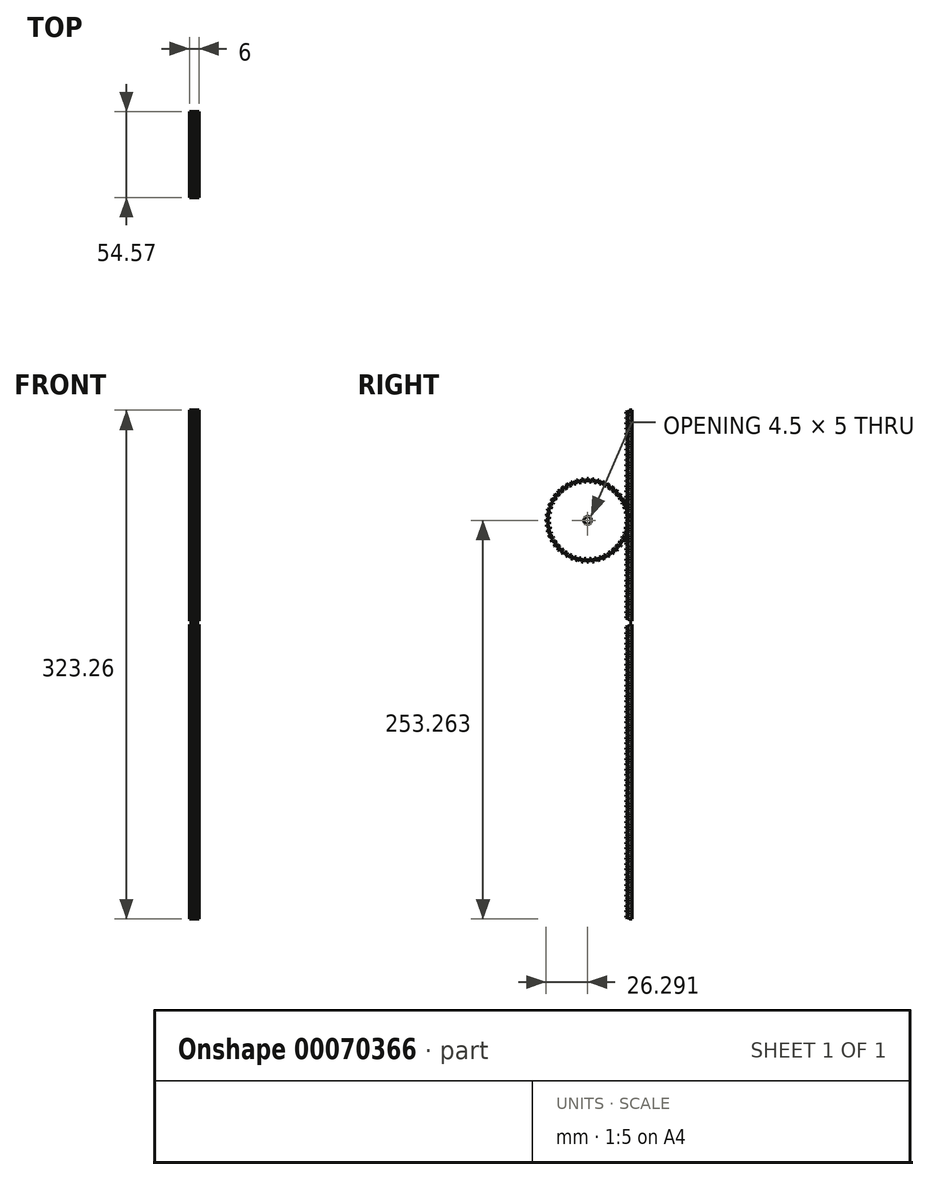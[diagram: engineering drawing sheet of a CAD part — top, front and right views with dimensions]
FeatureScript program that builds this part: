
annotation { "Feature Type Name" : "Feature", "Feature Type Description" : "" }
export const myFeature = defineFeature(function(context is Context, id is Id, definition is map)
    precondition{}
    {
        {
            var Q0;
            Q0=qCreatedBy(makeId("Right.planeOp"),FACE);
            var sketch = newSketch(context, id + "F0", { "sketchPlane" : qUnion([Q0])});
            skLineSegment(sketch, "E0", {"start": v(24.08, -5.55) * mm, "end": v(24.17, -5.13) * mm});
            skLineSegment(sketch, "E1", {"start": v(24.17, -5.13) * mm, "end": v(24.2, -4.7) * mm});
            skLineSegment(sketch, "E2", {"start": v(24.2, -4.7) * mm, "end": v(23.83, -4.49) * mm});
            skLineSegment(sketch, "E3", {"start": v(23.83, -4.49) * mm, "end": v(23.46, -4.3) * mm});
            skLineSegment(sketch, "E4", {"start": v(23.46, -4.3) * mm, "end": v(23.13, -4.14) * mm});
            skLineSegment(sketch, "E5", {"start": v(23.13, -4.14) * mm, "end": v(22.83, -4.01) * mm});
            skLineSegment(sketch, "E6", {"start": v(22.83, -4.01) * mm, "end": v(22.57, -3.91) * mm});
            skLineSegment(sketch, "E7", {"start": v(22.57, -3.91) * mm, "end": v(22.3, -3.83) * mm});
            skLineSegment(sketch, "E8", {"start": v(22.3, -3.83) * mm, "end": v(22.21, -3.78) * mm});
            skLineSegment(sketch, "E9", {"start": v(22.21, -3.78) * mm, "end": v(22.17, -3.73) * mm});
            skLineSegment(sketch, "E10", {"start": v(22.17, -3.73) * mm, "end": v(22.23, -2.79) * mm});
            skLineSegment(sketch, "E11", {"start": v(22.23, -2.79) * mm, "end": v(22.28, -2.75) * mm});
            skLineSegment(sketch, "E12", {"start": v(22.28, -2.75) * mm, "end": v(22.38, -2.71) * mm});
            skLineSegment(sketch, "E13", {"start": v(22.38, -2.71) * mm, "end": v(22.65, -2.66) * mm});
            skLineSegment(sketch, "E14", {"start": v(22.65, -2.66) * mm, "end": v(22.92, -2.6) * mm});
            skLineSegment(sketch, "E15", {"start": v(22.92, -2.6) * mm, "end": v(23.23, -2.52) * mm});
            skLineSegment(sketch, "E16", {"start": v(23.23, -2.52) * mm, "end": v(23.59, -2.4) * mm});
            skLineSegment(sketch, "E17", {"start": v(23.59, -2.4) * mm, "end": v(23.98, -2.26) * mm});
            skLineSegment(sketch, "E18", {"start": v(23.98, -2.26) * mm, "end": v(24.36, -2.1) * mm});
            skLineSegment(sketch, "E19", {"start": v(24.36, -2.1) * mm, "end": v(24.4, -1.67) * mm});
            skLineSegment(sketch, "E20", {"start": v(24.4, -1.67) * mm, "end": v(24.36, -1.23) * mm});
            skLineSegment(sketch, "E21", {"start": v(24.36, -1.23) * mm, "end": v(23.98, -1.07) * mm});
            skLineSegment(sketch, "E22", {"start": v(23.98, -1.07) * mm, "end": v(23.59, -0.93) * mm});
            skLineSegment(sketch, "E23", {"start": v(23.59, -0.93) * mm, "end": v(23.23, -0.82) * mm});
            skLineSegment(sketch, "E24", {"start": v(23.23, -0.82) * mm, "end": v(22.92, -0.73) * mm});
            skLineSegment(sketch, "E25", {"start": v(22.92, -0.73) * mm, "end": v(22.65, -0.67) * mm});
            skLineSegment(sketch, "E26", {"start": v(22.65, -0.67) * mm, "end": v(22.38, -0.62) * mm});
            skLineSegment(sketch, "E27", {"start": v(22.38, -0.62) * mm, "end": v(22.28, -0.59) * mm});
            skLineSegment(sketch, "E28", {"start": v(22.28, -0.59) * mm, "end": v(22.23, -0.55) * mm});
            skLineSegment(sketch, "E29", {"start": v(22.23, -0.55) * mm, "end": v(22.17, 0.4) * mm});
            skLineSegment(sketch, "E30", {"start": v(22.17, 0.4) * mm, "end": v(22.21, 0.45) * mm});
            skLineSegment(sketch, "E31", {"start": v(22.21, 0.45) * mm, "end": v(22.3, 0.5) * mm});
            skLineSegment(sketch, "E32", {"start": v(22.3, 0.5) * mm, "end": v(22.57, 0.58) * mm});
            skLineSegment(sketch, "E33", {"start": v(22.57, 0.58) * mm, "end": v(22.83, 0.68) * mm});
            skLineSegment(sketch, "E34", {"start": v(22.83, 0.68) * mm, "end": v(23.13, 0.8) * mm});
            skLineSegment(sketch, "E35", {"start": v(23.13, 0.8) * mm, "end": v(23.46, 0.96) * mm});
            skLineSegment(sketch, "E36", {"start": v(23.46, 0.96) * mm, "end": v(23.83, 1.15) * mm});
            skLineSegment(sketch, "E37", {"start": v(23.83, 1.15) * mm, "end": v(24.2, 1.36) * mm});
            skLineSegment(sketch, "E38", {"start": v(24.2, 1.36) * mm, "end": v(24.17, 1.8) * mm});
            skLineSegment(sketch, "E39", {"start": v(24.17, 1.8) * mm, "end": v(24.08, 2.22) * mm});
            skLineSegment(sketch, "E40", {"start": v(24.08, 2.22) * mm, "end": v(23.68, 2.33) * mm});
            skLineSegment(sketch, "E41", {"start": v(23.68, 2.33) * mm, "end": v(23.27, 2.42) * mm});
            skLineSegment(sketch, "E42", {"start": v(23.27, 2.42) * mm, "end": v(22.9, 2.49) * mm});
            skLineSegment(sketch, "E43", {"start": v(22.9, 2.49) * mm, "end": v(22.58, 2.53) * mm});
            skLineSegment(sketch, "E44", {"start": v(22.58, 2.53) * mm, "end": v(22.3, 2.55) * mm});
            skLineSegment(sketch, "E45", {"start": v(22.3, 2.55) * mm, "end": v(22.03, 2.57) * mm});
            skLineSegment(sketch, "E46", {"start": v(22.03, 2.57) * mm, "end": v(21.93, 2.59) * mm});
            skLineSegment(sketch, "E47", {"start": v(21.93, 2.59) * mm, "end": v(21.87, 2.62) * mm});
            skLineSegment(sketch, "E48", {"start": v(21.87, 2.62) * mm, "end": v(21.69, 3.56) * mm});
            skLineSegment(sketch, "E49", {"start": v(21.69, 3.56) * mm, "end": v(21.73, 3.6) * mm});
            skLineSegment(sketch, "E50", {"start": v(21.73, 3.6) * mm, "end": v(21.81, 3.67) * mm});
            skLineSegment(sketch, "E51", {"start": v(21.81, 3.67) * mm, "end": v(22.06, 3.79) * mm});
            skLineSegment(sketch, "E52", {"start": v(22.06, 3.79) * mm, "end": v(22.3, 3.91) * mm});
            skLineSegment(sketch, "E53", {"start": v(22.3, 3.91) * mm, "end": v(22.59, 4.08) * mm});
            skLineSegment(sketch, "E54", {"start": v(22.59, 4.08) * mm, "end": v(22.9, 4.28) * mm});
            skLineSegment(sketch, "E55", {"start": v(22.9, 4.28) * mm, "end": v(23.24, 4.52) * mm});
            skLineSegment(sketch, "E56", {"start": v(23.24, 4.52) * mm, "end": v(23.57, 4.77) * mm});
            skLineSegment(sketch, "E57", {"start": v(23.57, 4.77) * mm, "end": v(23.49, 5.2) * mm});
            skLineSegment(sketch, "E58", {"start": v(23.49, 5.2) * mm, "end": v(23.35, 5.6) * mm});
            skLineSegment(sketch, "E59", {"start": v(23.35, 5.6) * mm, "end": v(22.93, 5.67) * mm});
            skLineSegment(sketch, "E60", {"start": v(22.93, 5.67) * mm, "end": v(22.52, 5.7) * mm});
            skLineSegment(sketch, "E61", {"start": v(22.52, 5.7) * mm, "end": v(22.15, 5.72) * mm});
            skLineSegment(sketch, "E62", {"start": v(22.15, 5.72) * mm, "end": v(21.82, 5.72) * mm});
            skLineSegment(sketch, "E63", {"start": v(21.82, 5.72) * mm, "end": v(21.55, 5.7) * mm});
            skLineSegment(sketch, "E64", {"start": v(21.55, 5.7) * mm, "end": v(21.27, 5.69) * mm});
            skLineSegment(sketch, "E65", {"start": v(21.27, 5.69) * mm, "end": v(21.17, 5.7) * mm});
            skLineSegment(sketch, "E66", {"start": v(21.17, 5.7) * mm, "end": v(21.1, 5.72) * mm});
            skLineSegment(sketch, "E67", {"start": v(21.1, 5.72) * mm, "end": v(20.8, 6.62) * mm});
            skLineSegment(sketch, "E68", {"start": v(20.8, 6.62) * mm, "end": v(20.83, 6.68) * mm});
            skLineSegment(sketch, "E69", {"start": v(20.83, 6.68) * mm, "end": v(20.91, 6.75) * mm});
            skLineSegment(sketch, "E70", {"start": v(20.91, 6.75) * mm, "end": v(21.14, 6.9) * mm});
            skLineSegment(sketch, "E71", {"start": v(21.14, 6.9) * mm, "end": v(21.37, 7.06) * mm});
            skLineSegment(sketch, "E72", {"start": v(21.37, 7.06) * mm, "end": v(21.63, 7.26) * mm});
            skLineSegment(sketch, "E73", {"start": v(21.63, 7.26) * mm, "end": v(21.91, 7.5) * mm});
            skLineSegment(sketch, "E74", {"start": v(21.91, 7.5) * mm, "end": v(22.22, 7.78) * mm});
            skLineSegment(sketch, "E75", {"start": v(22.22, 7.78) * mm, "end": v(22.51, 8.07) * mm});
            skLineSegment(sketch, "E76", {"start": v(22.51, 8.07) * mm, "end": v(22.37, 8.48) * mm});
            skLineSegment(sketch, "E77", {"start": v(22.37, 8.48) * mm, "end": v(22.18, 8.87) * mm});
            skLineSegment(sketch, "E78", {"start": v(22.18, 8.87) * mm, "end": v(21.76, 8.87) * mm});
            skLineSegment(sketch, "E79", {"start": v(21.76, 8.87) * mm, "end": v(21.35, 8.86) * mm});
            skLineSegment(sketch, "E80", {"start": v(21.35, 8.86) * mm, "end": v(20.98, 8.83) * mm});
            skLineSegment(sketch, "E81", {"start": v(20.98, 8.83) * mm, "end": v(20.66, 8.78) * mm});
            skLineSegment(sketch, "E82", {"start": v(20.66, 8.78) * mm, "end": v(20.38, 8.74) * mm});
            skLineSegment(sketch, "E83", {"start": v(20.38, 8.74) * mm, "end": v(20.11, 8.68) * mm});
            skLineSegment(sketch, "E84", {"start": v(20.11, 8.68) * mm, "end": v(20, 8.67) * mm});
            skLineSegment(sketch, "E85", {"start": v(20, 8.67) * mm, "end": v(19.95, 8.7) * mm});
            skLineSegment(sketch, "E86", {"start": v(19.95, 8.7) * mm, "end": v(19.53, 9.54) * mm});
            skLineSegment(sketch, "E87", {"start": v(19.53, 9.54) * mm, "end": v(19.55, 9.6) * mm});
            skLineSegment(sketch, "E88", {"start": v(19.55, 9.6) * mm, "end": v(19.62, 9.68) * mm});
            skLineSegment(sketch, "E89", {"start": v(19.62, 9.68) * mm, "end": v(19.83, 9.86) * mm});
            skLineSegment(sketch, "E90", {"start": v(19.83, 9.86) * mm, "end": v(20.03, 10.05) * mm});
            skLineSegment(sketch, "E91", {"start": v(20.03, 10.05) * mm, "end": v(20.26, 10.28) * mm});
            skLineSegment(sketch, "E92", {"start": v(20.26, 10.28) * mm, "end": v(20.5, 10.55) * mm});
            skLineSegment(sketch, "E93", {"start": v(20.5, 10.55) * mm, "end": v(20.78, 10.87) * mm});
            skLineSegment(sketch, "E94", {"start": v(20.78, 10.87) * mm, "end": v(21.03, 11.2) * mm});
            skLineSegment(sketch, "E95", {"start": v(21.03, 11.2) * mm, "end": v(20.84, 11.6) * mm});
            skLineSegment(sketch, "E96", {"start": v(20.84, 11.6) * mm, "end": v(20.6, 11.96) * mm});
            skLineSegment(sketch, "E97", {"start": v(20.6, 11.96) * mm, "end": v(20.18, 11.9) * mm});
            skLineSegment(sketch, "E98", {"start": v(20.18, 11.9) * mm, "end": v(19.77, 11.83) * mm});
            skLineSegment(sketch, "E99", {"start": v(19.77, 11.83) * mm, "end": v(19.41, 11.75) * mm});
            skLineSegment(sketch, "E100", {"start": v(19.41, 11.75) * mm, "end": v(19.1, 11.67) * mm});
            skLineSegment(sketch, "E101", {"start": v(19.1, 11.67) * mm, "end": v(18.83, 11.59) * mm});
            skLineSegment(sketch, "E102", {"start": v(18.83, 11.59) * mm, "end": v(18.57, 11.5) * mm});
            skLineSegment(sketch, "E103", {"start": v(18.57, 11.5) * mm, "end": v(18.47, 11.47) * mm});
            skLineSegment(sketch, "E104", {"start": v(18.47, 11.47) * mm, "end": v(18.4, 11.49) * mm});
            skLineSegment(sketch, "E105", {"start": v(18.4, 11.49) * mm, "end": v(17.88, 12.27) * mm});
            skLineSegment(sketch, "E106", {"start": v(17.88, 12.27) * mm, "end": v(17.9, 12.34) * mm});
            skLineSegment(sketch, "E107", {"start": v(17.9, 12.34) * mm, "end": v(17.95, 12.43) * mm});
            skLineSegment(sketch, "E108", {"start": v(17.95, 12.43) * mm, "end": v(18.13, 12.63) * mm});
            skLineSegment(sketch, "E109", {"start": v(18.13, 12.63) * mm, "end": v(18.31, 12.84) * mm});
            skLineSegment(sketch, "E110", {"start": v(18.31, 12.84) * mm, "end": v(18.5, 13.1) * mm});
            skLineSegment(sketch, "E111", {"start": v(18.5, 13.1) * mm, "end": v(18.72, 13.4) * mm});
            skLineSegment(sketch, "E112", {"start": v(18.72, 13.4) * mm, "end": v(18.94, 13.76) * mm});
            skLineSegment(sketch, "E113", {"start": v(18.94, 13.76) * mm, "end": v(19.15, 14.12) * mm});
            skLineSegment(sketch, "E114", {"start": v(19.15, 14.12) * mm, "end": v(18.91, 14.48) * mm});
            skLineSegment(sketch, "E115", {"start": v(18.91, 14.48) * mm, "end": v(18.63, 14.8) * mm});
            skLineSegment(sketch, "E116", {"start": v(18.63, 14.8) * mm, "end": v(18.22, 14.7) * mm});
            skLineSegment(sketch, "E117", {"start": v(18.22, 14.7) * mm, "end": v(17.82, 14.58) * mm});
            skLineSegment(sketch, "E118", {"start": v(17.82, 14.58) * mm, "end": v(17.47, 14.45) * mm});
            skLineSegment(sketch, "E119", {"start": v(17.47, 14.45) * mm, "end": v(17.17, 14.33) * mm});
            skLineSegment(sketch, "E120", {"start": v(17.17, 14.33) * mm, "end": v(16.92, 14.2) * mm});
            skLineSegment(sketch, "E121", {"start": v(16.92, 14.2) * mm, "end": v(16.68, 14.08) * mm});
            skLineSegment(sketch, "E122", {"start": v(16.68, 14.08) * mm, "end": v(16.58, 14.05) * mm});
            skLineSegment(sketch, "E123", {"start": v(16.58, 14.05) * mm, "end": v(16.51, 14.05) * mm});
            skLineSegment(sketch, "E124", {"start": v(16.51, 14.05) * mm, "end": v(15.89, 14.77) * mm});
            skLineSegment(sketch, "E125", {"start": v(15.89, 14.77) * mm, "end": v(15.9, 14.83) * mm});
            skLineSegment(sketch, "E126", {"start": v(15.9, 14.83) * mm, "end": v(15.94, 14.93) * mm});
            skLineSegment(sketch, "E127", {"start": v(15.94, 14.93) * mm, "end": v(16.1, 15.15) * mm});
            skLineSegment(sketch, "E128", {"start": v(16.1, 15.15) * mm, "end": v(16.24, 15.39) * mm});
            skLineSegment(sketch, "E129", {"start": v(16.24, 15.39) * mm, "end": v(16.4, 15.67) * mm});
            skLineSegment(sketch, "E130", {"start": v(16.4, 15.67) * mm, "end": v(16.58, 16) * mm});
            skLineSegment(sketch, "E131", {"start": v(16.58, 16) * mm, "end": v(16.75, 16.38) * mm});
            skLineSegment(sketch, "E132", {"start": v(16.75, 16.38) * mm, "end": v(16.91, 16.76) * mm});
            skLineSegment(sketch, "E133", {"start": v(16.91, 16.76) * mm, "end": v(16.62, 17.09) * mm});
            skLineSegment(sketch, "E134", {"start": v(16.62, 17.09) * mm, "end": v(16.3, 17.38) * mm});
            skLineSegment(sketch, "E135", {"start": v(16.3, 17.38) * mm, "end": v(15.91, 17.22) * mm});
            skLineSegment(sketch, "E136", {"start": v(15.91, 17.22) * mm, "end": v(15.53, 17.04) * mm});
            skLineSegment(sketch, "E137", {"start": v(15.53, 17.04) * mm, "end": v(15.2, 16.87) * mm});
            skLineSegment(sketch, "E138", {"start": v(15.2, 16.87) * mm, "end": v(14.92, 16.7) * mm});
            skLineSegment(sketch, "E139", {"start": v(14.92, 16.7) * mm, "end": v(14.69, 16.56) * mm});
            skLineSegment(sketch, "E140", {"start": v(14.69, 16.56) * mm, "end": v(14.46, 16.4) * mm});
            skLineSegment(sketch, "E141", {"start": v(14.46, 16.4) * mm, "end": v(14.37, 16.36) * mm});
            skLineSegment(sketch, "E142", {"start": v(14.37, 16.36) * mm, "end": v(14.3, 16.35) * mm});
            skLineSegment(sketch, "E143", {"start": v(14.3, 16.35) * mm, "end": v(13.59, 16.98) * mm});
            skLineSegment(sketch, "E144", {"start": v(13.59, 16.98) * mm, "end": v(13.58, 17.04) * mm});
            skLineSegment(sketch, "E145", {"start": v(13.58, 17.04) * mm, "end": v(13.62, 17.14) * mm});
            skLineSegment(sketch, "E146", {"start": v(13.62, 17.14) * mm, "end": v(13.74, 17.39) * mm});
            skLineSegment(sketch, "E147", {"start": v(13.74, 17.39) * mm, "end": v(13.86, 17.64) * mm});
            skLineSegment(sketch, "E148", {"start": v(13.86, 17.64) * mm, "end": v(13.98, 17.94) * mm});
            skLineSegment(sketch, "E149", {"start": v(13.98, 17.94) * mm, "end": v(14.1, 18.29) * mm});
            skLineSegment(sketch, "E150", {"start": v(14.1, 18.29) * mm, "end": v(14.23, 18.69) * mm});
            skLineSegment(sketch, "E151", {"start": v(14.23, 18.69) * mm, "end": v(14.34, 19.1) * mm});
            skLineSegment(sketch, "E152", {"start": v(14.34, 19.1) * mm, "end": v(14.02, 19.38) * mm});
            skLineSegment(sketch, "E153", {"start": v(14.02, 19.38) * mm, "end": v(13.65, 19.62) * mm});
            skLineSegment(sketch, "E154", {"start": v(13.65, 19.62) * mm, "end": v(13.3, 19.4) * mm});
            skLineSegment(sketch, "E155", {"start": v(13.3, 19.4) * mm, "end": v(12.94, 19.19) * mm});
            skLineSegment(sketch, "E156", {"start": v(12.94, 19.19) * mm, "end": v(12.64, 18.97) * mm});
            skLineSegment(sketch, "E157", {"start": v(12.64, 18.97) * mm, "end": v(12.38, 18.78) * mm});
            skLineSegment(sketch, "E158", {"start": v(12.38, 18.78) * mm, "end": v(12.16, 18.6) * mm});
            skLineSegment(sketch, "E159", {"start": v(12.16, 18.6) * mm, "end": v(11.96, 18.41) * mm});
            skLineSegment(sketch, "E160", {"start": v(11.96, 18.41) * mm, "end": v(11.87, 18.36) * mm});
            skLineSegment(sketch, "E161", {"start": v(11.87, 18.36) * mm, "end": v(11.8, 18.34) * mm});
            skLineSegment(sketch, "E162", {"start": v(11.8, 18.34) * mm, "end": v(11.02, 18.87) * mm});
            skLineSegment(sketch, "E163", {"start": v(11.02, 18.87) * mm, "end": v(11, 18.93) * mm});
            skLineSegment(sketch, "E164", {"start": v(11, 18.93) * mm, "end": v(11.03, 19.04) * mm});
            skLineSegment(sketch, "E165", {"start": v(11.03, 19.04) * mm, "end": v(11.12, 19.3) * mm});
            skLineSegment(sketch, "E166", {"start": v(11.12, 19.3) * mm, "end": v(11.2, 19.56) * mm});
            skLineSegment(sketch, "E167", {"start": v(11.2, 19.56) * mm, "end": v(11.29, 19.88) * mm});
            skLineSegment(sketch, "E168", {"start": v(11.29, 19.88) * mm, "end": v(11.37, 20.24) * mm});
            skLineSegment(sketch, "E169", {"start": v(11.37, 20.24) * mm, "end": v(11.44, 20.65) * mm});
            skLineSegment(sketch, "E170", {"start": v(11.44, 20.65) * mm, "end": v(11.5, 21.06) * mm});
            skLineSegment(sketch, "E171", {"start": v(11.5, 21.06) * mm, "end": v(11.13, 21.3) * mm});
            skLineSegment(sketch, "E172", {"start": v(11.13, 21.3) * mm, "end": v(10.74, 21.5) * mm});
            skLineSegment(sketch, "E173", {"start": v(10.74, 21.5) * mm, "end": v(10.4, 21.24) * mm});
            skLineSegment(sketch, "E174", {"start": v(10.4, 21.24) * mm, "end": v(10.09, 20.98) * mm});
            skLineSegment(sketch, "E175", {"start": v(10.09, 20.98) * mm, "end": v(9.81, 20.73) * mm});
            skLineSegment(sketch, "E176", {"start": v(9.81, 20.73) * mm, "end": v(9.58, 20.5) * mm});
            skLineSegment(sketch, "E177", {"start": v(9.58, 20.5) * mm, "end": v(9.4, 20.3) * mm});
            skLineSegment(sketch, "E178", {"start": v(9.4, 20.3) * mm, "end": v(9.22, 20.08) * mm});
            skLineSegment(sketch, "E179", {"start": v(9.22, 20.08) * mm, "end": v(9.14, 20.01) * mm});
            skLineSegment(sketch, "E180", {"start": v(9.14, 20.01) * mm, "end": v(9.08, 20) * mm});
            skLineSegment(sketch, "E181", {"start": v(9.08, 20) * mm, "end": v(8.23, 20.41) * mm});
            skLineSegment(sketch, "E182", {"start": v(8.23, 20.41) * mm, "end": v(8.2, 20.47) * mm});
            skLineSegment(sketch, "E183", {"start": v(8.2, 20.47) * mm, "end": v(8.21, 20.58) * mm});
            skLineSegment(sketch, "E184", {"start": v(8.21, 20.58) * mm, "end": v(8.27, 20.85) * mm});
            skLineSegment(sketch, "E185", {"start": v(8.27, 20.85) * mm, "end": v(8.32, 21.12) * mm});
            skLineSegment(sketch, "E186", {"start": v(8.32, 21.12) * mm, "end": v(8.36, 21.44) * mm});
            skLineSegment(sketch, "E187", {"start": v(8.36, 21.44) * mm, "end": v(8.4, 21.81) * mm});
            skLineSegment(sketch, "E188", {"start": v(8.4, 21.81) * mm, "end": v(8.4, 22.23) * mm});
            skLineSegment(sketch, "E189", {"start": v(8.4, 22.23) * mm, "end": v(8.4, 22.65) * mm});
            skLineSegment(sketch, "E190", {"start": v(8.4, 22.65) * mm, "end": v(8.02, 22.84) * mm});
            skLineSegment(sketch, "E191", {"start": v(8.02, 22.84) * mm, "end": v(7.6, 22.98) * mm});
            skLineSegment(sketch, "E192", {"start": v(7.6, 22.98) * mm, "end": v(7.31, 22.68) * mm});
            skLineSegment(sketch, "E193", {"start": v(7.31, 22.68) * mm, "end": v(7.03, 22.38) * mm});
            skLineSegment(sketch, "E194", {"start": v(7.03, 22.38) * mm, "end": v(6.79, 22.1) * mm});
            skLineSegment(sketch, "E195", {"start": v(6.79, 22.1) * mm, "end": v(6.6, 21.84) * mm});
            skLineSegment(sketch, "E196", {"start": v(6.6, 21.84) * mm, "end": v(6.43, 21.6) * mm});
            skLineSegment(sketch, "E197", {"start": v(6.43, 21.6) * mm, "end": v(6.28, 21.38) * mm});
            skLineSegment(sketch, "E198", {"start": v(6.28, 21.38) * mm, "end": v(6.21, 21.3) * mm});
            skLineSegment(sketch, "E199", {"start": v(6.21, 21.3) * mm, "end": v(6.15, 21.27) * mm});
            skLineSegment(sketch, "E200", {"start": v(6.15, 21.27) * mm, "end": v(5.26, 21.57) * mm});
            skLineSegment(sketch, "E201", {"start": v(5.26, 21.57) * mm, "end": v(5.23, 21.63) * mm});
            skLineSegment(sketch, "E202", {"start": v(5.23, 21.63) * mm, "end": v(5.22, 21.74) * mm});
            skLineSegment(sketch, "E203", {"start": v(5.22, 21.74) * mm, "end": v(5.24, 22.01) * mm});
            skLineSegment(sketch, "E204", {"start": v(5.24, 22.01) * mm, "end": v(5.25, 22.3) * mm});
            skLineSegment(sketch, "E205", {"start": v(5.25, 22.3) * mm, "end": v(5.25, 22.61) * mm});
            skLineSegment(sketch, "E206", {"start": v(5.25, 22.61) * mm, "end": v(5.24, 22.99) * mm});
            skLineSegment(sketch, "E207", {"start": v(5.24, 22.99) * mm, "end": v(5.2, 23.4) * mm});
            skLineSegment(sketch, "E208", {"start": v(5.2, 23.4) * mm, "end": v(5.14, 23.82) * mm});
            skLineSegment(sketch, "E209", {"start": v(5.14, 23.82) * mm, "end": v(4.73, 23.96) * mm});
            skLineSegment(sketch, "E210", {"start": v(4.73, 23.96) * mm, "end": v(4.3, 24.04) * mm});
            skLineSegment(sketch, "E211", {"start": v(4.3, 24.04) * mm, "end": v(4.05, 23.7) * mm});
            skLineSegment(sketch, "E212", {"start": v(4.05, 23.7) * mm, "end": v(3.81, 23.37) * mm});
            skLineSegment(sketch, "E213", {"start": v(3.81, 23.37) * mm, "end": v(3.61, 23.05) * mm});
            skLineSegment(sketch, "E214", {"start": v(3.61, 23.05) * mm, "end": v(3.45, 22.77) * mm});
            skLineSegment(sketch, "E215", {"start": v(3.45, 22.77) * mm, "end": v(3.32, 22.53) * mm});
            skLineSegment(sketch, "E216", {"start": v(3.32, 22.53) * mm, "end": v(3.2, 22.28) * mm});
            skLineSegment(sketch, "E217", {"start": v(3.2, 22.28) * mm, "end": v(3.14, 22.2) * mm});
            skLineSegment(sketch, "E218", {"start": v(3.14, 22.2) * mm, "end": v(3.09, 22.16) * mm});
            skLineSegment(sketch, "E219", {"start": v(3.09, 22.16) * mm, "end": v(2.16, 22.34) * mm});
            skLineSegment(sketch, "E220", {"start": v(2.16, 22.34) * mm, "end": v(2.12, 22.4) * mm});
            skLineSegment(sketch, "E221", {"start": v(2.12, 22.4) * mm, "end": v(2.1, 22.5) * mm});
            skLineSegment(sketch, "E222", {"start": v(2.1, 22.5) * mm, "end": v(2.09, 22.77) * mm});
            skLineSegment(sketch, "E223", {"start": v(2.09, 22.77) * mm, "end": v(2.06, 23.05) * mm});
            skLineSegment(sketch, "E224", {"start": v(2.06, 23.05) * mm, "end": v(2.02, 23.37) * mm});
            skLineSegment(sketch, "E225", {"start": v(2.02, 23.37) * mm, "end": v(1.96, 23.74) * mm});
            skLineSegment(sketch, "E226", {"start": v(1.96, 23.74) * mm, "end": v(1.86, 24.14) * mm});
            skLineSegment(sketch, "E227", {"start": v(1.86, 24.14) * mm, "end": v(1.76, 24.55) * mm});
            skLineSegment(sketch, "E228", {"start": v(1.76, 24.55) * mm, "end": v(1.33, 24.63) * mm});
            skLineSegment(sketch, "E229", {"start": v(1.33, 24.63) * mm, "end": v(0.9, 24.66) * mm});
            skLineSegment(sketch, "E230", {"start": v(0.9, 24.66) * mm, "end": v(0.69, 24.3) * mm});
            skLineSegment(sketch, "E231", {"start": v(0.69, 24.3) * mm, "end": v(0.5, 23.93) * mm});
            skLineSegment(sketch, "E232", {"start": v(0.5, 23.93) * mm, "end": v(0.34, 23.6) * mm});
            skLineSegment(sketch, "E233", {"start": v(0.34, 23.6) * mm, "end": v(0.21, 23.3) * mm});
            skLineSegment(sketch, "E234", {"start": v(0.21, 23.3) * mm, "end": v(0.11, 23.03) * mm});
            skLineSegment(sketch, "E235", {"start": v(0.11, 23.03) * mm, "end": v(0.03, 22.77) * mm});
            skLineSegment(sketch, "E236", {"start": v(0.03, 22.77) * mm, "end": v(-0.02, 22.68) * mm});
            skLineSegment(sketch, "E237", {"start": v(-0.02, 22.68) * mm, "end": v(-0.06, 22.63) * mm});
            skLineSegment(sketch, "E238", {"start": v(-0.06, 22.63) * mm, "end": v(-1.01, 22.7) * mm});
            skLineSegment(sketch, "E239", {"start": v(-1.01, 22.7) * mm, "end": v(-1.05, 22.74) * mm});
            skLineSegment(sketch, "E240", {"start": v(-1.05, 22.74) * mm, "end": v(-1.09, 22.84) * mm});
            skLineSegment(sketch, "E241", {"start": v(-1.09, 22.84) * mm, "end": v(-1.14, 23.11) * mm});
            skLineSegment(sketch, "E242", {"start": v(-1.14, 23.11) * mm, "end": v(-1.2, 23.39) * mm});
            skLineSegment(sketch, "E243", {"start": v(-1.2, 23.39) * mm, "end": v(-1.28, 23.7) * mm});
            skLineSegment(sketch, "E244", {"start": v(-1.28, 23.7) * mm, "end": v(-1.4, 24.05) * mm});
            skLineSegment(sketch, "E245", {"start": v(-1.4, 24.05) * mm, "end": v(-1.54, 24.44) * mm});
            skLineSegment(sketch, "E246", {"start": v(-1.54, 24.44) * mm, "end": v(-1.7, 24.83) * mm});
            skLineSegment(sketch, "E247", {"start": v(-1.7, 24.83) * mm, "end": v(-2.13, 24.86) * mm});
            skLineSegment(sketch, "E248", {"start": v(-2.13, 24.86) * mm, "end": v(-2.57, 24.83) * mm});
            skLineSegment(sketch, "E249", {"start": v(-2.57, 24.83) * mm, "end": v(-2.73, 24.44) * mm});
            skLineSegment(sketch, "E250", {"start": v(-2.73, 24.44) * mm, "end": v(-2.87, 24.05) * mm});
            skLineSegment(sketch, "E251", {"start": v(-2.87, 24.05) * mm, "end": v(-2.98, 23.7) * mm});
            skLineSegment(sketch, "E252", {"start": v(-2.98, 23.7) * mm, "end": v(-3.07, 23.39) * mm});
            skLineSegment(sketch, "E253", {"start": v(-3.07, 23.39) * mm, "end": v(-3.13, 23.11) * mm});
            skLineSegment(sketch, "E254", {"start": v(-3.13, 23.11) * mm, "end": v(-3.18, 22.84) * mm});
            skLineSegment(sketch, "E255", {"start": v(-3.18, 22.84) * mm, "end": v(-3.21, 22.74) * mm});
            skLineSegment(sketch, "E256", {"start": v(-3.21, 22.74) * mm, "end": v(-3.25, 22.7) * mm});
            skLineSegment(sketch, "E257", {"start": v(-3.25, 22.7) * mm, "end": v(-4.2, 22.63) * mm});
            skLineSegment(sketch, "E258", {"start": v(-4.2, 22.63) * mm, "end": v(-4.25, 22.68) * mm});
            skLineSegment(sketch, "E259", {"start": v(-4.25, 22.68) * mm, "end": v(-4.3, 22.77) * mm});
            skLineSegment(sketch, "E260", {"start": v(-4.3, 22.77) * mm, "end": v(-4.38, 23.03) * mm});
            skLineSegment(sketch, "E261", {"start": v(-4.38, 23.03) * mm, "end": v(-4.48, 23.3) * mm});
            skLineSegment(sketch, "E262", {"start": v(-4.48, 23.3) * mm, "end": v(-4.6, 23.6) * mm});
            skLineSegment(sketch, "E263", {"start": v(-4.6, 23.6) * mm, "end": v(-4.76, 23.93) * mm});
            skLineSegment(sketch, "E264", {"start": v(-4.76, 23.93) * mm, "end": v(-4.95, 24.3) * mm});
            skLineSegment(sketch, "E265", {"start": v(-4.95, 24.3) * mm, "end": v(-5.16, 24.66) * mm});
            skLineSegment(sketch, "E266", {"start": v(-5.16, 24.66) * mm, "end": v(-5.6, 24.63) * mm});
            skLineSegment(sketch, "E267", {"start": v(-5.6, 24.63) * mm, "end": v(-6.02, 24.55) * mm});
            skLineSegment(sketch, "E268", {"start": v(-6.02, 24.55) * mm, "end": v(-6.13, 24.14) * mm});
            skLineSegment(sketch, "E269", {"start": v(-6.13, 24.14) * mm, "end": v(-6.22, 23.74) * mm});
            skLineSegment(sketch, "E270", {"start": v(-6.22, 23.74) * mm, "end": v(-6.29, 23.37) * mm});
            skLineSegment(sketch, "E271", {"start": v(-6.29, 23.37) * mm, "end": v(-6.33, 23.05) * mm});
            skLineSegment(sketch, "E272", {"start": v(-6.33, 23.05) * mm, "end": v(-6.35, 22.77) * mm});
            skLineSegment(sketch, "E273", {"start": v(-6.35, 22.77) * mm, "end": v(-6.37, 22.5) * mm});
            skLineSegment(sketch, "E274", {"start": v(-6.37, 22.5) * mm, "end": v(-6.39, 22.4) * mm});
            skLineSegment(sketch, "E275", {"start": v(-6.39, 22.4) * mm, "end": v(-6.42, 22.34) * mm});
            skLineSegment(sketch, "E276", {"start": v(-6.42, 22.34) * mm, "end": v(-7.35, 22.16) * mm});
            skLineSegment(sketch, "E277", {"start": v(-7.35, 22.16) * mm, "end": v(-7.4, 22.2) * mm});
            skLineSegment(sketch, "E278", {"start": v(-7.4, 22.2) * mm, "end": v(-7.47, 22.28) * mm});
            skLineSegment(sketch, "E279", {"start": v(-7.47, 22.28) * mm, "end": v(-7.58, 22.53) * mm});
            skLineSegment(sketch, "E280", {"start": v(-7.58, 22.53) * mm, "end": v(-7.71, 22.77) * mm});
            skLineSegment(sketch, "E281", {"start": v(-7.71, 22.77) * mm, "end": v(-7.88, 23.05) * mm});
            skLineSegment(sketch, "E282", {"start": v(-7.88, 23.05) * mm, "end": v(-8.08, 23.37) * mm});
            skLineSegment(sketch, "E283", {"start": v(-8.08, 23.37) * mm, "end": v(-8.32, 23.7) * mm});
            skLineSegment(sketch, "E284", {"start": v(-8.32, 23.7) * mm, "end": v(-8.57, 24.04) * mm});
            skLineSegment(sketch, "E285", {"start": v(-8.57, 24.04) * mm, "end": v(-9, 23.96) * mm});
            skLineSegment(sketch, "E286", {"start": v(-9, 23.96) * mm, "end": v(-9.4, 23.82) * mm});
            skLineSegment(sketch, "E287", {"start": v(-9.4, 23.82) * mm, "end": v(-9.46, 23.4) * mm});
            skLineSegment(sketch, "E288", {"start": v(-9.46, 23.4) * mm, "end": v(-9.5, 22.99) * mm});
            skLineSegment(sketch, "E289", {"start": v(-9.5, 22.99) * mm, "end": v(-9.52, 22.61) * mm});
            skLineSegment(sketch, "E290", {"start": v(-9.52, 22.61) * mm, "end": v(-9.52, 22.3) * mm});
            skLineSegment(sketch, "E291", {"start": v(-9.52, 22.3) * mm, "end": v(-9.5, 22.01) * mm});
            skLineSegment(sketch, "E292", {"start": v(-9.5, 22.01) * mm, "end": v(-9.48, 21.74) * mm});
            skLineSegment(sketch, "E293", {"start": v(-9.48, 21.74) * mm, "end": v(-9.5, 21.63) * mm});
            skLineSegment(sketch, "E294", {"start": v(-9.5, 21.63) * mm, "end": v(-9.52, 21.57) * mm});
            skLineSegment(sketch, "E295", {"start": v(-9.52, 21.57) * mm, "end": v(-10.42, 21.27) * mm});
            skLineSegment(sketch, "E296", {"start": v(-10.42, 21.27) * mm, "end": v(-10.48, 21.3) * mm});
            skLineSegment(sketch, "E297", {"start": v(-10.48, 21.3) * mm, "end": v(-10.55, 21.38) * mm});
            skLineSegment(sketch, "E298", {"start": v(-10.55, 21.38) * mm, "end": v(-10.7, 21.6) * mm});
            skLineSegment(sketch, "E299", {"start": v(-10.7, 21.6) * mm, "end": v(-10.86, 21.84) * mm});
            skLineSegment(sketch, "E300", {"start": v(-10.86, 21.84) * mm, "end": v(-11.05, 22.1) * mm});
            skLineSegment(sketch, "E301", {"start": v(-11.05, 22.1) * mm, "end": v(-11.3, 22.38) * mm});
            skLineSegment(sketch, "E302", {"start": v(-11.3, 22.38) * mm, "end": v(-11.58, 22.68) * mm});
            skLineSegment(sketch, "E303", {"start": v(-11.58, 22.68) * mm, "end": v(-11.87, 22.98) * mm});
            skLineSegment(sketch, "E304", {"start": v(-11.87, 22.98) * mm, "end": v(-12.28, 22.84) * mm});
            skLineSegment(sketch, "E305", {"start": v(-12.28, 22.84) * mm, "end": v(-12.67, 22.65) * mm});
            skLineSegment(sketch, "E306", {"start": v(-12.67, 22.65) * mm, "end": v(-12.67, 22.23) * mm});
            skLineSegment(sketch, "E307", {"start": v(-12.67, 22.23) * mm, "end": v(-12.66, 21.81) * mm});
            skLineSegment(sketch, "E308", {"start": v(-12.66, 21.81) * mm, "end": v(-12.62, 21.44) * mm});
            skLineSegment(sketch, "E309", {"start": v(-12.62, 21.44) * mm, "end": v(-12.58, 21.12) * mm});
            skLineSegment(sketch, "E310", {"start": v(-12.58, 21.12) * mm, "end": v(-12.54, 20.85) * mm});
            skLineSegment(sketch, "E311", {"start": v(-12.54, 20.85) * mm, "end": v(-12.48, 20.58) * mm});
            skLineSegment(sketch, "E312", {"start": v(-12.48, 20.58) * mm, "end": v(-12.47, 20.47) * mm});
            skLineSegment(sketch, "E313", {"start": v(-12.47, 20.47) * mm, "end": v(-12.5, 20.41) * mm});
            skLineSegment(sketch, "E314", {"start": v(-12.5, 20.41) * mm, "end": v(-13.34, 20) * mm});
            skLineSegment(sketch, "E315", {"start": v(-13.34, 20) * mm, "end": v(-13.4, 20.01) * mm});
            skLineSegment(sketch, "E316", {"start": v(-13.4, 20.01) * mm, "end": v(-13.48, 20.08) * mm});
            skLineSegment(sketch, "E317", {"start": v(-13.48, 20.08) * mm, "end": v(-13.66, 20.3) * mm});
            skLineSegment(sketch, "E318", {"start": v(-13.66, 20.3) * mm, "end": v(-13.85, 20.5) * mm});
            skLineSegment(sketch, "E319", {"start": v(-13.85, 20.5) * mm, "end": v(-14.08, 20.73) * mm});
            skLineSegment(sketch, "E320", {"start": v(-14.08, 20.73) * mm, "end": v(-14.35, 20.98) * mm});
            skLineSegment(sketch, "E321", {"start": v(-14.35, 20.98) * mm, "end": v(-14.67, 21.24) * mm});
            skLineSegment(sketch, "E322", {"start": v(-14.67, 21.24) * mm, "end": v(-15, 21.5) * mm});
            skLineSegment(sketch, "E323", {"start": v(-15, 21.5) * mm, "end": v(-15.4, 21.3) * mm});
            skLineSegment(sketch, "E324", {"start": v(-15.4, 21.3) * mm, "end": v(-15.76, 21.06) * mm});
            skLineSegment(sketch, "E325", {"start": v(-15.76, 21.06) * mm, "end": v(-15.7, 20.65) * mm});
            skLineSegment(sketch, "E326", {"start": v(-15.7, 20.65) * mm, "end": v(-15.63, 20.24) * mm});
            skLineSegment(sketch, "E327", {"start": v(-15.63, 20.24) * mm, "end": v(-15.55, 19.88) * mm});
            skLineSegment(sketch, "E328", {"start": v(-15.55, 19.88) * mm, "end": v(-15.47, 19.56) * mm});
            skLineSegment(sketch, "E329", {"start": v(-15.47, 19.56) * mm, "end": v(-15.38, 19.3) * mm});
            skLineSegment(sketch, "E330", {"start": v(-15.38, 19.3) * mm, "end": v(-15.3, 19.04) * mm});
            skLineSegment(sketch, "E331", {"start": v(-15.3, 19.04) * mm, "end": v(-15.27, 18.93) * mm});
            skLineSegment(sketch, "E332", {"start": v(-15.27, 18.93) * mm, "end": v(-15.28, 18.87) * mm});
            skLineSegment(sketch, "E333", {"start": v(-15.28, 18.87) * mm, "end": v(-16.07, 18.34) * mm});
            skLineSegment(sketch, "E334", {"start": v(-16.07, 18.34) * mm, "end": v(-16.14, 18.36) * mm});
            skLineSegment(sketch, "E335", {"start": v(-16.14, 18.36) * mm, "end": v(-16.22, 18.41) * mm});
            skLineSegment(sketch, "E336", {"start": v(-16.22, 18.41) * mm, "end": v(-16.43, 18.6) * mm});
            skLineSegment(sketch, "E337", {"start": v(-16.43, 18.6) * mm, "end": v(-16.64, 18.78) * mm});
            skLineSegment(sketch, "E338", {"start": v(-16.64, 18.78) * mm, "end": v(-16.9, 18.97) * mm});
            skLineSegment(sketch, "E339", {"start": v(-16.9, 18.97) * mm, "end": v(-17.2, 19.19) * mm});
            skLineSegment(sketch, "E340", {"start": v(-17.2, 19.19) * mm, "end": v(-17.56, 19.4) * mm});
            skLineSegment(sketch, "E341", {"start": v(-17.56, 19.4) * mm, "end": v(-17.92, 19.62) * mm});
            skLineSegment(sketch, "E342", {"start": v(-17.92, 19.62) * mm, "end": v(-18.28, 19.38) * mm});
            skLineSegment(sketch, "E343", {"start": v(-18.28, 19.38) * mm, "end": v(-18.6, 19.1) * mm});
            skLineSegment(sketch, "E344", {"start": v(-18.6, 19.1) * mm, "end": v(-18.5, 18.69) * mm});
            skLineSegment(sketch, "E345", {"start": v(-18.5, 18.69) * mm, "end": v(-18.37, 18.29) * mm});
            skLineSegment(sketch, "E346", {"start": v(-18.37, 18.29) * mm, "end": v(-18.25, 17.94) * mm});
            skLineSegment(sketch, "E347", {"start": v(-18.25, 17.94) * mm, "end": v(-18.12, 17.64) * mm});
            skLineSegment(sketch, "E348", {"start": v(-18.12, 17.64) * mm, "end": v(-18, 17.39) * mm});
            skLineSegment(sketch, "E349", {"start": v(-18, 17.39) * mm, "end": v(-17.88, 17.14) * mm});
            skLineSegment(sketch, "E350", {"start": v(-17.88, 17.14) * mm, "end": v(-17.85, 17.04) * mm});
            skLineSegment(sketch, "E351", {"start": v(-17.85, 17.04) * mm, "end": v(-17.85, 16.98) * mm});
            skLineSegment(sketch, "E352", {"start": v(-17.85, 16.98) * mm, "end": v(-18.57, 16.35) * mm});
            skLineSegment(sketch, "E353", {"start": v(-18.57, 16.35) * mm, "end": v(-18.63, 16.36) * mm});
            skLineSegment(sketch, "E354", {"start": v(-18.63, 16.36) * mm, "end": v(-18.73, 16.4) * mm});
            skLineSegment(sketch, "E355", {"start": v(-18.73, 16.4) * mm, "end": v(-18.95, 16.56) * mm});
            skLineSegment(sketch, "E356", {"start": v(-18.95, 16.56) * mm, "end": v(-19.19, 16.7) * mm});
            skLineSegment(sketch, "E357", {"start": v(-19.19, 16.7) * mm, "end": v(-19.47, 16.87) * mm});
            skLineSegment(sketch, "E358", {"start": v(-19.47, 16.87) * mm, "end": v(-19.8, 17.04) * mm});
            skLineSegment(sketch, "E359", {"start": v(-19.8, 17.04) * mm, "end": v(-20.17, 17.22) * mm});
            skLineSegment(sketch, "E360", {"start": v(-20.17, 17.22) * mm, "end": v(-20.56, 17.38) * mm});
            skLineSegment(sketch, "E361", {"start": v(-20.56, 17.38) * mm, "end": v(-20.89, 17.09) * mm});
            skLineSegment(sketch, "E362", {"start": v(-20.89, 17.09) * mm, "end": v(-21.17, 16.76) * mm});
            skLineSegment(sketch, "E363", {"start": v(-21.17, 16.76) * mm, "end": v(-21.02, 16.38) * mm});
            skLineSegment(sketch, "E364", {"start": v(-21.02, 16.38) * mm, "end": v(-20.84, 16) * mm});
            skLineSegment(sketch, "E365", {"start": v(-20.84, 16) * mm, "end": v(-20.67, 15.67) * mm});
            skLineSegment(sketch, "E366", {"start": v(-20.67, 15.67) * mm, "end": v(-20.5, 15.39) * mm});
            skLineSegment(sketch, "E367", {"start": v(-20.5, 15.39) * mm, "end": v(-20.36, 15.15) * mm});
            skLineSegment(sketch, "E368", {"start": v(-20.36, 15.15) * mm, "end": v(-20.2, 14.93) * mm});
            skLineSegment(sketch, "E369", {"start": v(-20.2, 14.93) * mm, "end": v(-20.16, 14.83) * mm});
            skLineSegment(sketch, "E370", {"start": v(-20.16, 14.83) * mm, "end": v(-20.15, 14.77) * mm});
            skLineSegment(sketch, "E371", {"start": v(-20.15, 14.77) * mm, "end": v(-20.78, 14.05) * mm});
            skLineSegment(sketch, "E372", {"start": v(-20.78, 14.05) * mm, "end": v(-20.84, 14.05) * mm});
            skLineSegment(sketch, "E373", {"start": v(-20.84, 14.05) * mm, "end": v(-20.94, 14.08) * mm});
            skLineSegment(sketch, "E374", {"start": v(-20.94, 14.08) * mm, "end": v(-21.19, 14.2) * mm});
            skLineSegment(sketch, "E375", {"start": v(-21.19, 14.2) * mm, "end": v(-21.44, 14.33) * mm});
            skLineSegment(sketch, "E376", {"start": v(-21.44, 14.33) * mm, "end": v(-21.74, 14.45) * mm});
            skLineSegment(sketch, "E377", {"start": v(-21.74, 14.45) * mm, "end": v(-22.09, 14.58) * mm});
            skLineSegment(sketch, "E378", {"start": v(-22.09, 14.58) * mm, "end": v(-22.49, 14.7) * mm});
            skLineSegment(sketch, "E379", {"start": v(-22.49, 14.7) * mm, "end": v(-22.9, 14.8) * mm});
            skLineSegment(sketch, "E380", {"start": v(-22.9, 14.8) * mm, "end": v(-23.18, 14.48) * mm});
            skLineSegment(sketch, "E381", {"start": v(-23.18, 14.48) * mm, "end": v(-23.42, 14.12) * mm});
            skLineSegment(sketch, "E382", {"start": v(-23.42, 14.12) * mm, "end": v(-23.2, 13.76) * mm});
            skLineSegment(sketch, "E383", {"start": v(-23.2, 13.76) * mm, "end": v(-22.99, 13.4) * mm});
            skLineSegment(sketch, "E384", {"start": v(-22.99, 13.4) * mm, "end": v(-22.77, 13.1) * mm});
            skLineSegment(sketch, "E385", {"start": v(-22.77, 13.1) * mm, "end": v(-22.58, 12.84) * mm});
            skLineSegment(sketch, "E386", {"start": v(-22.58, 12.84) * mm, "end": v(-22.4, 12.63) * mm});
            skLineSegment(sketch, "E387", {"start": v(-22.4, 12.63) * mm, "end": v(-22.21, 12.43) * mm});
            skLineSegment(sketch, "E388", {"start": v(-22.21, 12.43) * mm, "end": v(-22.16, 12.34) * mm});
            skLineSegment(sketch, "E389", {"start": v(-22.16, 12.34) * mm, "end": v(-22.14, 12.27) * mm});
            skLineSegment(sketch, "E390", {"start": v(-22.14, 12.27) * mm, "end": v(-22.67, 11.49) * mm});
            skLineSegment(sketch, "E391", {"start": v(-22.67, 11.49) * mm, "end": v(-22.73, 11.47) * mm});
            skLineSegment(sketch, "E392", {"start": v(-22.73, 11.47) * mm, "end": v(-22.84, 11.5) * mm});
            skLineSegment(sketch, "E393", {"start": v(-22.84, 11.5) * mm, "end": v(-23.1, 11.59) * mm});
            skLineSegment(sketch, "E394", {"start": v(-23.1, 11.59) * mm, "end": v(-23.36, 11.67) * mm});
            skLineSegment(sketch, "E395", {"start": v(-23.36, 11.67) * mm, "end": v(-23.68, 11.75) * mm});
            skLineSegment(sketch, "E396", {"start": v(-23.68, 11.75) * mm, "end": v(-24.04, 11.83) * mm});
            skLineSegment(sketch, "E397", {"start": v(-24.04, 11.83) * mm, "end": v(-24.45, 11.9) * mm});
            skLineSegment(sketch, "E398", {"start": v(-24.45, 11.9) * mm, "end": v(-24.86, 11.96) * mm});
            skLineSegment(sketch, "E399", {"start": v(-24.86, 11.96) * mm, "end": v(-25.1, 11.6) * mm});
            skLineSegment(sketch, "E400", {"start": v(-25.1, 11.6) * mm, "end": v(-25.3, 11.2) * mm});
            skLineSegment(sketch, "E401", {"start": v(-25.3, 11.2) * mm, "end": v(-25.04, 10.87) * mm});
            skLineSegment(sketch, "E402", {"start": v(-25.04, 10.87) * mm, "end": v(-24.77, 10.55) * mm});
            skLineSegment(sketch, "E403", {"start": v(-24.77, 10.55) * mm, "end": v(-24.52, 10.28) * mm});
            skLineSegment(sketch, "E404", {"start": v(-24.52, 10.28) * mm, "end": v(-24.3, 10.05) * mm});
            skLineSegment(sketch, "E405", {"start": v(-24.3, 10.05) * mm, "end": v(-24.1, 9.86) * mm});
            skLineSegment(sketch, "E406", {"start": v(-24.1, 9.86) * mm, "end": v(-23.88, 9.68) * mm});
            skLineSegment(sketch, "E407", {"start": v(-23.88, 9.68) * mm, "end": v(-23.81, 9.6) * mm});
            skLineSegment(sketch, "E408", {"start": v(-23.81, 9.6) * mm, "end": v(-23.8, 9.54) * mm});
            skLineSegment(sketch, "E409", {"start": v(-23.8, 9.54) * mm, "end": v(-24.21, 8.7) * mm});
            skLineSegment(sketch, "E410", {"start": v(-24.21, 8.7) * mm, "end": v(-24.27, 8.67) * mm});
            skLineSegment(sketch, "E411", {"start": v(-24.27, 8.67) * mm, "end": v(-24.38, 8.68) * mm});
            skLineSegment(sketch, "E412", {"start": v(-24.38, 8.68) * mm, "end": v(-24.65, 8.74) * mm});
            skLineSegment(sketch, "E413", {"start": v(-24.65, 8.74) * mm, "end": v(-24.92, 8.78) * mm});
            skLineSegment(sketch, "E414", {"start": v(-24.92, 8.78) * mm, "end": v(-25.24, 8.83) * mm});
            skLineSegment(sketch, "E415", {"start": v(-25.24, 8.83) * mm, "end": v(-25.61, 8.86) * mm});
            skLineSegment(sketch, "E416", {"start": v(-25.61, 8.86) * mm, "end": v(-26.03, 8.87) * mm});
            skLineSegment(sketch, "E417", {"start": v(-26.03, 8.87) * mm, "end": v(-26.45, 8.87) * mm});
            skLineSegment(sketch, "E418", {"start": v(-26.45, 8.87) * mm, "end": v(-26.64, 8.48) * mm});
            skLineSegment(sketch, "E419", {"start": v(-26.64, 8.48) * mm, "end": v(-26.78, 8.07) * mm});
            skLineSegment(sketch, "E420", {"start": v(-26.78, 8.07) * mm, "end": v(-26.48, 7.78) * mm});
            skLineSegment(sketch, "E421", {"start": v(-26.48, 7.78) * mm, "end": v(-26.18, 7.5) * mm});
            skLineSegment(sketch, "E422", {"start": v(-26.18, 7.5) * mm, "end": v(-25.9, 7.26) * mm});
            skLineSegment(sketch, "E423", {"start": v(-25.9, 7.26) * mm, "end": v(-25.64, 7.06) * mm});
            skLineSegment(sketch, "E424", {"start": v(-25.64, 7.06) * mm, "end": v(-25.4, 6.9) * mm});
            skLineSegment(sketch, "E425", {"start": v(-25.4, 6.9) * mm, "end": v(-25.18, 6.75) * mm});
            skLineSegment(sketch, "E426", {"start": v(-25.18, 6.75) * mm, "end": v(-25.1, 6.68) * mm});
            skLineSegment(sketch, "E427", {"start": v(-25.1, 6.68) * mm, "end": v(-25.07, 6.62) * mm});
            skLineSegment(sketch, "E428", {"start": v(-25.07, 6.62) * mm, "end": v(-25.37, 5.72) * mm});
            skLineSegment(sketch, "E429", {"start": v(-25.37, 5.72) * mm, "end": v(-25.43, 5.7) * mm});
            skLineSegment(sketch, "E430", {"start": v(-25.43, 5.7) * mm, "end": v(-25.54, 5.69) * mm});
            skLineSegment(sketch, "E431", {"start": v(-25.54, 5.69) * mm, "end": v(-25.81, 5.7) * mm});
            skLineSegment(sketch, "E432", {"start": v(-25.81, 5.7) * mm, "end": v(-26.09, 5.72) * mm});
            skLineSegment(sketch, "E433", {"start": v(-26.09, 5.72) * mm, "end": v(-26.41, 5.72) * mm});
            skLineSegment(sketch, "E434", {"start": v(-26.41, 5.72) * mm, "end": v(-26.78, 5.7) * mm});
            skLineSegment(sketch, "E435", {"start": v(-26.78, 5.7) * mm, "end": v(-27.2, 5.67) * mm});
            skLineSegment(sketch, "E436", {"start": v(-27.2, 5.67) * mm, "end": v(-27.62, 5.6) * mm});
            skLineSegment(sketch, "E437", {"start": v(-27.62, 5.6) * mm, "end": v(-27.75, 5.2) * mm});
            skLineSegment(sketch, "E438", {"start": v(-27.75, 5.2) * mm, "end": v(-27.84, 4.77) * mm});
            skLineSegment(sketch, "E439", {"start": v(-27.84, 4.77) * mm, "end": v(-27.5, 4.52) * mm});
            skLineSegment(sketch, "E440", {"start": v(-27.5, 4.52) * mm, "end": v(-27.17, 4.28) * mm});
            skLineSegment(sketch, "E441", {"start": v(-27.17, 4.28) * mm, "end": v(-26.85, 4.08) * mm});
            skLineSegment(sketch, "E442", {"start": v(-26.85, 4.08) * mm, "end": v(-26.57, 3.91) * mm});
            skLineSegment(sketch, "E443", {"start": v(-26.57, 3.91) * mm, "end": v(-26.33, 3.79) * mm});
            skLineSegment(sketch, "E444", {"start": v(-26.33, 3.79) * mm, "end": v(-26.08, 3.67) * mm});
            skLineSegment(sketch, "E445", {"start": v(-26.08, 3.67) * mm, "end": v(-26, 3.6) * mm});
            skLineSegment(sketch, "E446", {"start": v(-26, 3.6) * mm, "end": v(-25.95, 3.56) * mm});
            skLineSegment(sketch, "E447", {"start": v(-25.95, 3.56) * mm, "end": v(-26.14, 2.62) * mm});
            skLineSegment(sketch, "E448", {"start": v(-26.14, 2.62) * mm, "end": v(-26.2, 2.59) * mm});
            skLineSegment(sketch, "E449", {"start": v(-26.2, 2.59) * mm, "end": v(-26.3, 2.57) * mm});
            skLineSegment(sketch, "E450", {"start": v(-26.3, 2.57) * mm, "end": v(-26.57, 2.55) * mm});
            skLineSegment(sketch, "E451", {"start": v(-26.57, 2.55) * mm, "end": v(-26.85, 2.53) * mm});
            skLineSegment(sketch, "E452", {"start": v(-26.85, 2.53) * mm, "end": v(-27.17, 2.49) * mm});
            skLineSegment(sketch, "E453", {"start": v(-27.17, 2.49) * mm, "end": v(-27.54, 2.42) * mm});
            skLineSegment(sketch, "E454", {"start": v(-27.54, 2.42) * mm, "end": v(-27.94, 2.33) * mm});
            skLineSegment(sketch, "E455", {"start": v(-27.94, 2.33) * mm, "end": v(-28.35, 2.22) * mm});
            skLineSegment(sketch, "E456", {"start": v(-28.35, 2.22) * mm, "end": v(-28.43, 1.8) * mm});
            skLineSegment(sketch, "E457", {"start": v(-28.43, 1.8) * mm, "end": v(-28.46, 1.36) * mm});
            skLineSegment(sketch, "E458", {"start": v(-28.46, 1.36) * mm, "end": v(-28.1, 1.15) * mm});
            skLineSegment(sketch, "E459", {"start": v(-28.1, 1.15) * mm, "end": v(-27.73, 0.96) * mm});
            skLineSegment(sketch, "E460", {"start": v(-27.73, 0.96) * mm, "end": v(-27.4, 0.8) * mm});
            skLineSegment(sketch, "E461", {"start": v(-27.4, 0.8) * mm, "end": v(-27.1, 0.68) * mm});
            skLineSegment(sketch, "E462", {"start": v(-27.1, 0.68) * mm, "end": v(-26.83, 0.58) * mm});
            skLineSegment(sketch, "E463", {"start": v(-26.83, 0.58) * mm, "end": v(-26.57, 0.5) * mm});
            skLineSegment(sketch, "E464", {"start": v(-26.57, 0.5) * mm, "end": v(-26.48, 0.45) * mm});
            skLineSegment(sketch, "E465", {"start": v(-26.48, 0.45) * mm, "end": v(-26.43, 0.4) * mm});
            skLineSegment(sketch, "E466", {"start": v(-26.43, 0.4) * mm, "end": v(-26.5, -0.55) * mm});
            skLineSegment(sketch, "E467", {"start": v(-26.5, -0.55) * mm, "end": v(-26.54, -0.59) * mm});
            skLineSegment(sketch, "E468", {"start": v(-26.54, -0.59) * mm, "end": v(-26.64, -0.62) * mm});
            skLineSegment(sketch, "E469", {"start": v(-26.64, -0.62) * mm, "end": v(-26.91, -0.67) * mm});
            skLineSegment(sketch, "E470", {"start": v(-26.91, -0.67) * mm, "end": v(-27.18, -0.73) * mm});
            skLineSegment(sketch, "E471", {"start": v(-27.18, -0.73) * mm, "end": v(-27.5, -0.82) * mm});
            skLineSegment(sketch, "E472", {"start": v(-27.5, -0.82) * mm, "end": v(-27.85, -0.93) * mm});
            skLineSegment(sketch, "E473", {"start": v(-27.85, -0.93) * mm, "end": v(-28.24, -1.07) * mm});
            skLineSegment(sketch, "E474", {"start": v(-28.24, -1.07) * mm, "end": v(-28.63, -1.23) * mm});
            skLineSegment(sketch, "E475", {"start": v(-28.63, -1.23) * mm, "end": v(-28.66, -1.67) * mm});
            skLineSegment(sketch, "E476", {"start": v(-28.66, -1.67) * mm, "end": v(-28.63, -2.1) * mm});
            skLineSegment(sketch, "E477", {"start": v(-28.63, -2.1) * mm, "end": v(-28.24, -2.26) * mm});
            skLineSegment(sketch, "E478", {"start": v(-28.24, -2.26) * mm, "end": v(-27.85, -2.4) * mm});
            skLineSegment(sketch, "E479", {"start": v(-27.85, -2.4) * mm, "end": v(-27.5, -2.52) * mm});
            skLineSegment(sketch, "E480", {"start": v(-27.5, -2.52) * mm, "end": v(-27.18, -2.6) * mm});
            skLineSegment(sketch, "E481", {"start": v(-27.18, -2.6) * mm, "end": v(-26.91, -2.66) * mm});
            skLineSegment(sketch, "E482", {"start": v(-26.91, -2.66) * mm, "end": v(-26.64, -2.71) * mm});
            skLineSegment(sketch, "E483", {"start": v(-26.64, -2.71) * mm, "end": v(-26.54, -2.75) * mm});
            skLineSegment(sketch, "E484", {"start": v(-26.54, -2.75) * mm, "end": v(-26.5, -2.79) * mm});
            skLineSegment(sketch, "E485", {"start": v(-26.5, -2.79) * mm, "end": v(-26.43, -3.73) * mm});
            skLineSegment(sketch, "E486", {"start": v(-26.43, -3.73) * mm, "end": v(-26.48, -3.78) * mm});
            skLineSegment(sketch, "E487", {"start": v(-26.48, -3.78) * mm, "end": v(-26.57, -3.83) * mm});
            skLineSegment(sketch, "E488", {"start": v(-26.57, -3.83) * mm, "end": v(-26.83, -3.91) * mm});
            skLineSegment(sketch, "E489", {"start": v(-26.83, -3.91) * mm, "end": v(-27.1, -4.01) * mm});
            skLineSegment(sketch, "E490", {"start": v(-27.1, -4.01) * mm, "end": v(-27.4, -4.14) * mm});
            skLineSegment(sketch, "E491", {"start": v(-27.4, -4.14) * mm, "end": v(-27.73, -4.3) * mm});
            skLineSegment(sketch, "E492", {"start": v(-27.73, -4.3) * mm, "end": v(-28.1, -4.49) * mm});
            skLineSegment(sketch, "E493", {"start": v(-28.1, -4.49) * mm, "end": v(-28.46, -4.7) * mm});
            skLineSegment(sketch, "E494", {"start": v(-28.46, -4.7) * mm, "end": v(-28.43, -5.13) * mm});
            skLineSegment(sketch, "E495", {"start": v(-28.43, -5.13) * mm, "end": v(-28.35, -5.55) * mm});
            skLineSegment(sketch, "E496", {"start": v(-28.35, -5.55) * mm, "end": v(-27.94, -5.66) * mm});
            skLineSegment(sketch, "E497", {"start": v(-27.94, -5.66) * mm, "end": v(-27.54, -5.75) * mm});
            skLineSegment(sketch, "E498", {"start": v(-27.54, -5.75) * mm, "end": v(-27.17, -5.82) * mm});
            skLineSegment(sketch, "E499", {"start": v(-27.17, -5.82) * mm, "end": v(-26.85, -5.86) * mm});
            skLineSegment(sketch, "E500", {"start": v(-26.85, -5.86) * mm, "end": v(-26.57, -5.89) * mm});
            skLineSegment(sketch, "E501", {"start": v(-26.57, -5.89) * mm, "end": v(-26.3, -5.9) * mm});
            skLineSegment(sketch, "E502", {"start": v(-26.3, -5.9) * mm, "end": v(-26.2, -5.92) * mm});
            skLineSegment(sketch, "E503", {"start": v(-26.2, -5.92) * mm, "end": v(-26.14, -5.96) * mm});
            skLineSegment(sketch, "E504", {"start": v(-26.14, -5.96) * mm, "end": v(-25.95, -6.89) * mm});
            skLineSegment(sketch, "E505", {"start": v(-25.95, -6.89) * mm, "end": v(-26, -6.94) * mm});
            skLineSegment(sketch, "E506", {"start": v(-26, -6.94) * mm, "end": v(-26.08, -7) * mm});
            skLineSegment(sketch, "E507", {"start": v(-26.08, -7) * mm, "end": v(-26.33, -7.12) * mm});
            skLineSegment(sketch, "E508", {"start": v(-26.33, -7.12) * mm, "end": v(-26.57, -7.25) * mm});
            skLineSegment(sketch, "E509", {"start": v(-26.57, -7.25) * mm, "end": v(-26.85, -7.41) * mm});
            skLineSegment(sketch, "E510", {"start": v(-26.85, -7.41) * mm, "end": v(-27.17, -7.61) * mm});
            skLineSegment(sketch, "E511", {"start": v(-27.17, -7.61) * mm, "end": v(-27.5, -7.85) * mm});
            skLineSegment(sketch, "E512", {"start": v(-27.5, -7.85) * mm, "end": v(-27.84, -8.1) * mm});
            skLineSegment(sketch, "E513", {"start": v(-27.84, -8.1) * mm, "end": v(-27.75, -8.53) * mm});
            skLineSegment(sketch, "E514", {"start": v(-27.75, -8.53) * mm, "end": v(-27.62, -8.94) * mm});
            skLineSegment(sketch, "E515", {"start": v(-27.62, -8.94) * mm, "end": v(-27.2, -9) * mm});
            skLineSegment(sketch, "E516", {"start": v(-27.2, -9) * mm, "end": v(-26.78, -9.04) * mm});
            skLineSegment(sketch, "E517", {"start": v(-26.78, -9.04) * mm, "end": v(-26.41, -9.05) * mm});
            skLineSegment(sketch, "E518", {"start": v(-26.41, -9.05) * mm, "end": v(-26.09, -9.05) * mm});
            skLineSegment(sketch, "E519", {"start": v(-26.09, -9.05) * mm, "end": v(-25.81, -9.04) * mm});
            skLineSegment(sketch, "E520", {"start": v(-25.81, -9.04) * mm, "end": v(-25.54, -9.02) * mm});
            skLineSegment(sketch, "E521", {"start": v(-25.54, -9.02) * mm, "end": v(-25.43, -9.03) * mm});
            skLineSegment(sketch, "E522", {"start": v(-25.43, -9.03) * mm, "end": v(-25.37, -9.06) * mm});
            skLineSegment(sketch, "E523", {"start": v(-25.37, -9.06) * mm, "end": v(-25.07, -9.95) * mm});
            skLineSegment(sketch, "E524", {"start": v(-25.07, -9.95) * mm, "end": v(-25.1, -10.01) * mm});
            skLineSegment(sketch, "E525", {"start": v(-25.1, -10.01) * mm, "end": v(-25.18, -10.08) * mm});
            skLineSegment(sketch, "E526", {"start": v(-25.18, -10.08) * mm, "end": v(-25.4, -10.23) * mm});
            skLineSegment(sketch, "E527", {"start": v(-25.4, -10.23) * mm, "end": v(-25.64, -10.4) * mm});
            skLineSegment(sketch, "E528", {"start": v(-25.64, -10.4) * mm, "end": v(-25.9, -10.59) * mm});
            skLineSegment(sketch, "E529", {"start": v(-25.9, -10.59) * mm, "end": v(-26.18, -10.83) * mm});
            skLineSegment(sketch, "E530", {"start": v(-26.18, -10.83) * mm, "end": v(-26.48, -11.1) * mm});
            skLineSegment(sketch, "E531", {"start": v(-26.48, -11.1) * mm, "end": v(-26.78, -11.4) * mm});
            skLineSegment(sketch, "E532", {"start": v(-26.78, -11.4) * mm, "end": v(-26.64, -11.82) * mm});
            skLineSegment(sketch, "E533", {"start": v(-26.64, -11.82) * mm, "end": v(-26.45, -12.2) * mm});
            skLineSegment(sketch, "E534", {"start": v(-26.45, -12.2) * mm, "end": v(-26.03, -12.2) * mm});
            skLineSegment(sketch, "E535", {"start": v(-26.03, -12.2) * mm, "end": v(-25.61, -12.2) * mm});
            skLineSegment(sketch, "E536", {"start": v(-25.61, -12.2) * mm, "end": v(-25.24, -12.16) * mm});
            skLineSegment(sketch, "E537", {"start": v(-25.24, -12.16) * mm, "end": v(-24.92, -12.12) * mm});
            skLineSegment(sketch, "E538", {"start": v(-24.92, -12.12) * mm, "end": v(-24.65, -12.07) * mm});
            skLineSegment(sketch, "E539", {"start": v(-24.65, -12.07) * mm, "end": v(-24.38, -12.01) * mm});
            skLineSegment(sketch, "E540", {"start": v(-24.38, -12.01) * mm, "end": v(-24.27, -12) * mm});
            skLineSegment(sketch, "E541", {"start": v(-24.27, -12) * mm, "end": v(-24.21, -12.03) * mm});
            skLineSegment(sketch, "E542", {"start": v(-24.21, -12.03) * mm, "end": v(-23.8, -12.88) * mm});
            skLineSegment(sketch, "E543", {"start": v(-23.8, -12.88) * mm, "end": v(-23.81, -12.94) * mm});
            skLineSegment(sketch, "E544", {"start": v(-23.81, -12.94) * mm, "end": v(-23.88, -13.02) * mm});
            skLineSegment(sketch, "E545", {"start": v(-23.88, -13.02) * mm, "end": v(-24.1, -13.2) * mm});
            skLineSegment(sketch, "E546", {"start": v(-24.1, -13.2) * mm, "end": v(-24.3, -13.38) * mm});
            skLineSegment(sketch, "E547", {"start": v(-24.3, -13.38) * mm, "end": v(-24.52, -13.61) * mm});
            skLineSegment(sketch, "E548", {"start": v(-24.52, -13.61) * mm, "end": v(-24.77, -13.89) * mm});
            skLineSegment(sketch, "E549", {"start": v(-24.77, -13.89) * mm, "end": v(-25.04, -14.2) * mm});
            skLineSegment(sketch, "E550", {"start": v(-25.04, -14.2) * mm, "end": v(-25.3, -14.54) * mm});
            skLineSegment(sketch, "E551", {"start": v(-25.3, -14.54) * mm, "end": v(-25.1, -14.93) * mm});
            skLineSegment(sketch, "E552", {"start": v(-25.1, -14.93) * mm, "end": v(-24.86, -15.3) * mm});
            skLineSegment(sketch, "E553", {"start": v(-24.86, -15.3) * mm, "end": v(-24.45, -15.24) * mm});
            skLineSegment(sketch, "E554", {"start": v(-24.45, -15.24) * mm, "end": v(-24.04, -15.16) * mm});
            skLineSegment(sketch, "E555", {"start": v(-24.04, -15.16) * mm, "end": v(-23.68, -15.09) * mm});
            skLineSegment(sketch, "E556", {"start": v(-23.68, -15.09) * mm, "end": v(-23.36, -15) * mm});
            skLineSegment(sketch, "E557", {"start": v(-23.36, -15) * mm, "end": v(-23.1, -14.92) * mm});
            skLineSegment(sketch, "E558", {"start": v(-23.1, -14.92) * mm, "end": v(-22.84, -14.83) * mm});
            skLineSegment(sketch, "E559", {"start": v(-22.84, -14.83) * mm, "end": v(-22.73, -14.8) * mm});
            skLineSegment(sketch, "E560", {"start": v(-22.73, -14.8) * mm, "end": v(-22.67, -14.82) * mm});
            skLineSegment(sketch, "E561", {"start": v(-22.67, -14.82) * mm, "end": v(-22.14, -15.6) * mm});
            skLineSegment(sketch, "E562", {"start": v(-22.14, -15.6) * mm, "end": v(-22.16, -15.67) * mm});
            skLineSegment(sketch, "E563", {"start": v(-22.16, -15.67) * mm, "end": v(-22.21, -15.76) * mm});
            skLineSegment(sketch, "E564", {"start": v(-22.21, -15.76) * mm, "end": v(-22.4, -15.96) * mm});
            skLineSegment(sketch, "E565", {"start": v(-22.4, -15.96) * mm, "end": v(-22.58, -16.18) * mm});
            skLineSegment(sketch, "E566", {"start": v(-22.58, -16.18) * mm, "end": v(-22.77, -16.43) * mm});
            skLineSegment(sketch, "E567", {"start": v(-22.77, -16.43) * mm, "end": v(-22.99, -16.74) * mm});
            skLineSegment(sketch, "E568", {"start": v(-22.99, -16.74) * mm, "end": v(-23.2, -17.1) * mm});
            skLineSegment(sketch, "E569", {"start": v(-23.2, -17.1) * mm, "end": v(-23.42, -17.45) * mm});
            skLineSegment(sketch, "E570", {"start": v(-23.42, -17.45) * mm, "end": v(-23.18, -17.81) * mm});
            skLineSegment(sketch, "E571", {"start": v(-23.18, -17.81) * mm, "end": v(-22.9, -18.14) * mm});
            skLineSegment(sketch, "E572", {"start": v(-22.9, -18.14) * mm, "end": v(-22.49, -18.03) * mm});
            skLineSegment(sketch, "E573", {"start": v(-22.49, -18.03) * mm, "end": v(-22.09, -17.9) * mm});
            skLineSegment(sketch, "E574", {"start": v(-22.09, -17.9) * mm, "end": v(-21.74, -17.78) * mm});
            skLineSegment(sketch, "E575", {"start": v(-21.74, -17.78) * mm, "end": v(-21.44, -17.66) * mm});
            skLineSegment(sketch, "E576", {"start": v(-21.44, -17.66) * mm, "end": v(-21.19, -17.54) * mm});
            skLineSegment(sketch, "E577", {"start": v(-21.19, -17.54) * mm, "end": v(-20.94, -17.42) * mm});
            skLineSegment(sketch, "E578", {"start": v(-20.94, -17.42) * mm, "end": v(-20.84, -17.38) * mm});
            skLineSegment(sketch, "E579", {"start": v(-20.84, -17.38) * mm, "end": v(-20.78, -17.39) * mm});
            skLineSegment(sketch, "E580", {"start": v(-20.78, -17.39) * mm, "end": v(-20.15, -18.1) * mm});
            skLineSegment(sketch, "E581", {"start": v(-20.15, -18.1) * mm, "end": v(-20.16, -18.17) * mm});
            skLineSegment(sketch, "E582", {"start": v(-20.16, -18.17) * mm, "end": v(-20.2, -18.26) * mm});
            skLineSegment(sketch, "E583", {"start": v(-20.2, -18.26) * mm, "end": v(-20.36, -18.48) * mm});
            skLineSegment(sketch, "E584", {"start": v(-20.36, -18.48) * mm, "end": v(-20.5, -18.72) * mm});
            skLineSegment(sketch, "E585", {"start": v(-20.5, -18.72) * mm, "end": v(-20.67, -19) * mm});
            skLineSegment(sketch, "E586", {"start": v(-20.67, -19) * mm, "end": v(-20.84, -19.33) * mm});
            skLineSegment(sketch, "E587", {"start": v(-20.84, -19.33) * mm, "end": v(-21.02, -19.7) * mm});
            skLineSegment(sketch, "E588", {"start": v(-21.02, -19.7) * mm, "end": v(-21.17, -20.1) * mm});
            skLineSegment(sketch, "E589", {"start": v(-21.17, -20.1) * mm, "end": v(-20.89, -20.42) * mm});
            skLineSegment(sketch, "E590", {"start": v(-20.89, -20.42) * mm, "end": v(-20.56, -20.7) * mm});
            skLineSegment(sketch, "E591", {"start": v(-20.56, -20.7) * mm, "end": v(-20.17, -20.55) * mm});
            skLineSegment(sketch, "E592", {"start": v(-20.17, -20.55) * mm, "end": v(-19.8, -20.37) * mm});
            skLineSegment(sketch, "E593", {"start": v(-19.8, -20.37) * mm, "end": v(-19.47, -20.2) * mm});
            skLineSegment(sketch, "E594", {"start": v(-19.47, -20.2) * mm, "end": v(-19.19, -20.04) * mm});
            skLineSegment(sketch, "E595", {"start": v(-19.19, -20.04) * mm, "end": v(-18.95, -19.9) * mm});
            skLineSegment(sketch, "E596", {"start": v(-18.95, -19.9) * mm, "end": v(-18.73, -19.74) * mm});
            skLineSegment(sketch, "E597", {"start": v(-18.73, -19.74) * mm, "end": v(-18.63, -19.7) * mm});
            skLineSegment(sketch, "E598", {"start": v(-18.63, -19.7) * mm, "end": v(-18.57, -19.69) * mm});
            skLineSegment(sketch, "E599", {"start": v(-18.57, -19.69) * mm, "end": v(-17.85, -20.31) * mm});
            skLineSegment(sketch, "E600", {"start": v(-17.85, -20.31) * mm, "end": v(-17.85, -20.38) * mm});
            skLineSegment(sketch, "E601", {"start": v(-17.85, -20.38) * mm, "end": v(-17.88, -20.48) * mm});
            skLineSegment(sketch, "E602", {"start": v(-17.88, -20.48) * mm, "end": v(-18, -20.72) * mm});
            skLineSegment(sketch, "E603", {"start": v(-18, -20.72) * mm, "end": v(-18.12, -20.97) * mm});
            skLineSegment(sketch, "E604", {"start": v(-18.12, -20.97) * mm, "end": v(-18.25, -21.27) * mm});
            skLineSegment(sketch, "E605", {"start": v(-18.25, -21.27) * mm, "end": v(-18.37, -21.62) * mm});
            skLineSegment(sketch, "E606", {"start": v(-18.37, -21.62) * mm, "end": v(-18.5, -22.02) * mm});
            skLineSegment(sketch, "E607", {"start": v(-18.5, -22.02) * mm, "end": v(-18.6, -22.43) * mm});
            skLineSegment(sketch, "E608", {"start": v(-18.6, -22.43) * mm, "end": v(-18.28, -22.71) * mm});
            skLineSegment(sketch, "E609", {"start": v(-18.28, -22.71) * mm, "end": v(-17.92, -22.95) * mm});
            skLineSegment(sketch, "E610", {"start": v(-17.92, -22.95) * mm, "end": v(-17.56, -22.74) * mm});
            skLineSegment(sketch, "E611", {"start": v(-17.56, -22.74) * mm, "end": v(-17.2, -22.52) * mm});
            skLineSegment(sketch, "E612", {"start": v(-17.2, -22.52) * mm, "end": v(-16.9, -22.3) * mm});
            skLineSegment(sketch, "E613", {"start": v(-16.9, -22.3) * mm, "end": v(-16.64, -22.11) * mm});
            skLineSegment(sketch, "E614", {"start": v(-16.64, -22.11) * mm, "end": v(-16.43, -21.93) * mm});
            skLineSegment(sketch, "E615", {"start": v(-16.43, -21.93) * mm, "end": v(-16.22, -21.75) * mm});
            skLineSegment(sketch, "E616", {"start": v(-16.22, -21.75) * mm, "end": v(-16.14, -21.69) * mm});
            skLineSegment(sketch, "E617", {"start": v(-16.14, -21.69) * mm, "end": v(-16.07, -21.68) * mm});
            skLineSegment(sketch, "E618", {"start": v(-16.07, -21.68) * mm, "end": v(-15.28, -22.2) * mm});
            skLineSegment(sketch, "E619", {"start": v(-15.28, -22.2) * mm, "end": v(-15.27, -22.27) * mm});
            skLineSegment(sketch, "E620", {"start": v(-15.27, -22.27) * mm, "end": v(-15.3, -22.37) * mm});
            skLineSegment(sketch, "E621", {"start": v(-15.3, -22.37) * mm, "end": v(-15.38, -22.63) * mm});
            skLineSegment(sketch, "E622", {"start": v(-15.38, -22.63) * mm, "end": v(-15.47, -22.9) * mm});
            skLineSegment(sketch, "E623", {"start": v(-15.47, -22.9) * mm, "end": v(-15.55, -23.2) * mm});
            skLineSegment(sketch, "E624", {"start": v(-15.55, -23.2) * mm, "end": v(-15.63, -23.57) * mm});
            skLineSegment(sketch, "E625", {"start": v(-15.63, -23.57) * mm, "end": v(-15.7, -23.98) * mm});
            skLineSegment(sketch, "E626", {"start": v(-15.7, -23.98) * mm, "end": v(-15.76, -24.4) * mm});
            skLineSegment(sketch, "E627", {"start": v(-15.76, -24.4) * mm, "end": v(-15.4, -24.64) * mm});
            skLineSegment(sketch, "E628", {"start": v(-15.4, -24.64) * mm, "end": v(-15, -24.83) * mm});
            skLineSegment(sketch, "E629", {"start": v(-15, -24.83) * mm, "end": v(-14.67, -24.58) * mm});
            skLineSegment(sketch, "E630", {"start": v(-14.67, -24.58) * mm, "end": v(-14.35, -24.3) * mm});
            skLineSegment(sketch, "E631", {"start": v(-14.35, -24.3) * mm, "end": v(-14.08, -24.06) * mm});
            skLineSegment(sketch, "E632", {"start": v(-14.08, -24.06) * mm, "end": v(-13.85, -23.83) * mm});
            skLineSegment(sketch, "E633", {"start": v(-13.85, -23.83) * mm, "end": v(-13.66, -23.62) * mm});
            skLineSegment(sketch, "E634", {"start": v(-13.66, -23.62) * mm, "end": v(-13.48, -23.41) * mm});
            skLineSegment(sketch, "E635", {"start": v(-13.48, -23.41) * mm, "end": v(-13.4, -23.35) * mm});
            skLineSegment(sketch, "E636", {"start": v(-13.4, -23.35) * mm, "end": v(-13.34, -23.33) * mm});
            skLineSegment(sketch, "E637", {"start": v(-13.34, -23.33) * mm, "end": v(-12.5, -23.74) * mm});
            skLineSegment(sketch, "E638", {"start": v(-12.5, -23.74) * mm, "end": v(-12.47, -23.8) * mm});
            skLineSegment(sketch, "E639", {"start": v(-12.47, -23.8) * mm, "end": v(-12.48, -23.91) * mm});
            skLineSegment(sketch, "E640", {"start": v(-12.48, -23.91) * mm, "end": v(-12.54, -24.18) * mm});
            skLineSegment(sketch, "E641", {"start": v(-12.54, -24.18) * mm, "end": v(-12.58, -24.45) * mm});
            skLineSegment(sketch, "E642", {"start": v(-12.58, -24.45) * mm, "end": v(-12.62, -24.78) * mm});
            skLineSegment(sketch, "E643", {"start": v(-12.62, -24.78) * mm, "end": v(-12.66, -25.15) * mm});
            skLineSegment(sketch, "E644", {"start": v(-12.66, -25.15) * mm, "end": v(-12.67, -25.56) * mm});
            skLineSegment(sketch, "E645", {"start": v(-12.67, -25.56) * mm, "end": v(-12.67, -25.98) * mm});
            skLineSegment(sketch, "E646", {"start": v(-12.67, -25.98) * mm, "end": v(-12.28, -26.17) * mm});
            skLineSegment(sketch, "E647", {"start": v(-12.28, -26.17) * mm, "end": v(-11.87, -26.31) * mm});
            skLineSegment(sketch, "E648", {"start": v(-11.87, -26.31) * mm, "end": v(-11.58, -26.02) * mm});
            skLineSegment(sketch, "E649", {"start": v(-11.58, -26.02) * mm, "end": v(-11.3, -25.71) * mm});
            skLineSegment(sketch, "E650", {"start": v(-11.3, -25.71) * mm, "end": v(-11.05, -25.43) * mm});
            skLineSegment(sketch, "E651", {"start": v(-11.05, -25.43) * mm, "end": v(-10.86, -25.17) * mm});
            skLineSegment(sketch, "E652", {"start": v(-10.86, -25.17) * mm, "end": v(-10.7, -24.94) * mm});
            skLineSegment(sketch, "E653", {"start": v(-10.7, -24.94) * mm, "end": v(-10.55, -24.7) * mm});
            skLineSegment(sketch, "E654", {"start": v(-10.55, -24.7) * mm, "end": v(-10.48, -24.63) * mm});
            skLineSegment(sketch, "E655", {"start": v(-10.48, -24.63) * mm, "end": v(-10.42, -24.6) * mm});
            skLineSegment(sketch, "E656", {"start": v(-10.42, -24.6) * mm, "end": v(-9.52, -24.9) * mm});
            skLineSegment(sketch, "E657", {"start": v(-9.52, -24.9) * mm, "end": v(-9.5, -24.97) * mm});
            skLineSegment(sketch, "E658", {"start": v(-9.5, -24.97) * mm, "end": v(-9.48, -25.07) * mm});
            skLineSegment(sketch, "E659", {"start": v(-9.48, -25.07) * mm, "end": v(-9.5, -25.34) * mm});
            skLineSegment(sketch, "E660", {"start": v(-9.5, -25.34) * mm, "end": v(-9.52, -25.62) * mm});
            skLineSegment(sketch, "E661", {"start": v(-9.52, -25.62) * mm, "end": v(-9.52, -25.95) * mm});
            skLineSegment(sketch, "E662", {"start": v(-9.52, -25.95) * mm, "end": v(-9.5, -26.32) * mm});
            skLineSegment(sketch, "E663", {"start": v(-9.5, -26.32) * mm, "end": v(-9.46, -26.73) * mm});
            skLineSegment(sketch, "E664", {"start": v(-9.46, -26.73) * mm, "end": v(-9.4, -27.15) * mm});
            skLineSegment(sketch, "E665", {"start": v(-9.4, -27.15) * mm, "end": v(-9, -27.29) * mm});
            skLineSegment(sketch, "E666", {"start": v(-9, -27.29) * mm, "end": v(-8.57, -27.37) * mm});
            skLineSegment(sketch, "E667", {"start": v(-8.57, -27.37) * mm, "end": v(-8.32, -27.04) * mm});
            skLineSegment(sketch, "E668", {"start": v(-8.32, -27.04) * mm, "end": v(-8.08, -26.7) * mm});
            skLineSegment(sketch, "E669", {"start": v(-8.08, -26.7) * mm, "end": v(-7.88, -26.39) * mm});
            skLineSegment(sketch, "E670", {"start": v(-7.88, -26.39) * mm, "end": v(-7.71, -26.1) * mm});
            skLineSegment(sketch, "E671", {"start": v(-7.71, -26.1) * mm, "end": v(-7.58, -25.86) * mm});
            skLineSegment(sketch, "E672", {"start": v(-7.58, -25.86) * mm, "end": v(-7.47, -25.61) * mm});
            skLineSegment(sketch, "E673", {"start": v(-7.47, -25.61) * mm, "end": v(-7.4, -25.52) * mm});
            skLineSegment(sketch, "E674", {"start": v(-7.4, -25.52) * mm, "end": v(-7.35, -25.49) * mm});
            skLineSegment(sketch, "E675", {"start": v(-7.35, -25.49) * mm, "end": v(-6.42, -25.67) * mm});
            skLineSegment(sketch, "E676", {"start": v(-6.42, -25.67) * mm, "end": v(-6.39, -25.73) * mm});
            skLineSegment(sketch, "E677", {"start": v(-6.39, -25.73) * mm, "end": v(-6.37, -25.83) * mm});
            skLineSegment(sketch, "E678", {"start": v(-6.37, -25.83) * mm, "end": v(-6.35, -26.1) * mm});
            skLineSegment(sketch, "E679", {"start": v(-6.35, -26.1) * mm, "end": v(-6.33, -26.38) * mm});
            skLineSegment(sketch, "E680", {"start": v(-6.33, -26.38) * mm, "end": v(-6.29, -26.7) * mm});
            skLineSegment(sketch, "E681", {"start": v(-6.29, -26.7) * mm, "end": v(-6.22, -27.07) * mm});
            skLineSegment(sketch, "E682", {"start": v(-6.22, -27.07) * mm, "end": v(-6.13, -27.48) * mm});
            skLineSegment(sketch, "E683", {"start": v(-6.13, -27.48) * mm, "end": v(-6.02, -27.88) * mm});
            skLineSegment(sketch, "E684", {"start": v(-6.02, -27.88) * mm, "end": v(-5.6, -27.97) * mm});
            skLineSegment(sketch, "E685", {"start": v(-5.6, -27.97) * mm, "end": v(-5.16, -28) * mm});
            skLineSegment(sketch, "E686", {"start": v(-5.16, -28) * mm, "end": v(-4.95, -27.63) * mm});
            skLineSegment(sketch, "E687", {"start": v(-4.95, -27.63) * mm, "end": v(-4.76, -27.26) * mm});
            skLineSegment(sketch, "E688", {"start": v(-4.76, -27.26) * mm, "end": v(-4.6, -26.93) * mm});
            skLineSegment(sketch, "E689", {"start": v(-4.6, -26.93) * mm, "end": v(-4.48, -26.63) * mm});
            skLineSegment(sketch, "E690", {"start": v(-4.48, -26.63) * mm, "end": v(-4.38, -26.36) * mm});
            skLineSegment(sketch, "E691", {"start": v(-4.38, -26.36) * mm, "end": v(-4.3, -26.1) * mm});
            skLineSegment(sketch, "E692", {"start": v(-4.3, -26.1) * mm, "end": v(-4.25, -26) * mm});
            skLineSegment(sketch, "E693", {"start": v(-4.25, -26) * mm, "end": v(-4.2, -25.97) * mm});
            skLineSegment(sketch, "E694", {"start": v(-4.2, -25.97) * mm, "end": v(-3.25, -26.03) * mm});
            skLineSegment(sketch, "E695", {"start": v(-3.25, -26.03) * mm, "end": v(-3.21, -26.08) * mm});
            skLineSegment(sketch, "E696", {"start": v(-3.21, -26.08) * mm, "end": v(-3.18, -26.18) * mm});
            skLineSegment(sketch, "E697", {"start": v(-3.18, -26.18) * mm, "end": v(-3.13, -26.45) * mm});
            skLineSegment(sketch, "E698", {"start": v(-3.13, -26.45) * mm, "end": v(-3.07, -26.72) * mm});
            skLineSegment(sketch, "E699", {"start": v(-3.07, -26.72) * mm, "end": v(-2.98, -27.03) * mm});
            skLineSegment(sketch, "E700", {"start": v(-2.98, -27.03) * mm, "end": v(-2.87, -27.39) * mm});
            skLineSegment(sketch, "E701", {"start": v(-2.87, -27.39) * mm, "end": v(-2.73, -27.78) * mm});
            skLineSegment(sketch, "E702", {"start": v(-2.73, -27.78) * mm, "end": v(-2.57, -28.16) * mm});
            skLineSegment(sketch, "E703", {"start": v(-2.57, -28.16) * mm, "end": v(-2.13, -28.2) * mm});
            skLineSegment(sketch, "E704", {"start": v(-2.13, -28.2) * mm, "end": v(-1.7, -28.16) * mm});
            skLineSegment(sketch, "E705", {"start": v(-1.7, -28.16) * mm, "end": v(-1.54, -27.78) * mm});
            skLineSegment(sketch, "E706", {"start": v(-1.54, -27.78) * mm, "end": v(-1.4, -27.39) * mm});
            skLineSegment(sketch, "E707", {"start": v(-1.4, -27.39) * mm, "end": v(-1.28, -27.03) * mm});
            skLineSegment(sketch, "E708", {"start": v(-1.28, -27.03) * mm, "end": v(-1.2, -26.72) * mm});
            skLineSegment(sketch, "E709", {"start": v(-1.2, -26.72) * mm, "end": v(-1.14, -26.45) * mm});
            skLineSegment(sketch, "E710", {"start": v(-1.14, -26.45) * mm, "end": v(-1.09, -26.18) * mm});
            skLineSegment(sketch, "E711", {"start": v(-1.09, -26.18) * mm, "end": v(-1.05, -26.08) * mm});
            skLineSegment(sketch, "E712", {"start": v(-1.05, -26.08) * mm, "end": v(-1.01, -26.03) * mm});
            skLineSegment(sketch, "E713", {"start": v(-1.01, -26.03) * mm, "end": v(-0.06, -25.97) * mm});
            skLineSegment(sketch, "E714", {"start": v(-0.06, -25.97) * mm, "end": v(-0.02, -26) * mm});
            skLineSegment(sketch, "E715", {"start": v(-0.02, -26) * mm, "end": v(0.03, -26.1) * mm});
            skLineSegment(sketch, "E716", {"start": v(0.03, -26.1) * mm, "end": v(0.11, -26.36) * mm});
            skLineSegment(sketch, "E717", {"start": v(0.11, -26.36) * mm, "end": v(0.21, -26.63) * mm});
            skLineSegment(sketch, "E718", {"start": v(0.21, -26.63) * mm, "end": v(0.34, -26.93) * mm});
            skLineSegment(sketch, "E719", {"start": v(0.34, -26.93) * mm, "end": v(0.5, -27.26) * mm});
            skLineSegment(sketch, "E720", {"start": v(0.5, -27.26) * mm, "end": v(0.69, -27.63) * mm});
            skLineSegment(sketch, "E721", {"start": v(0.69, -27.63) * mm, "end": v(0.9, -28) * mm});
            skLineSegment(sketch, "E722", {"start": v(0.9, -28) * mm, "end": v(1.33, -27.97) * mm});
            skLineSegment(sketch, "E723", {"start": v(1.33, -27.97) * mm, "end": v(1.76, -27.88) * mm});
            skLineSegment(sketch, "E724", {"start": v(1.76, -27.88) * mm, "end": v(1.86, -27.48) * mm});
            skLineSegment(sketch, "E725", {"start": v(1.86, -27.48) * mm, "end": v(1.96, -27.07) * mm});
            skLineSegment(sketch, "E726", {"start": v(1.96, -27.07) * mm, "end": v(2.02, -26.7) * mm});
            skLineSegment(sketch, "E727", {"start": v(2.02, -26.7) * mm, "end": v(2.06, -26.38) * mm});
            skLineSegment(sketch, "E728", {"start": v(2.06, -26.38) * mm, "end": v(2.09, -26.1) * mm});
            skLineSegment(sketch, "E729", {"start": v(2.09, -26.1) * mm, "end": v(2.1, -25.83) * mm});
            skLineSegment(sketch, "E730", {"start": v(2.1, -25.83) * mm, "end": v(2.12, -25.73) * mm});
            skLineSegment(sketch, "E731", {"start": v(2.12, -25.73) * mm, "end": v(2.16, -25.67) * mm});
            skLineSegment(sketch, "E732", {"start": v(2.16, -25.67) * mm, "end": v(3.09, -25.49) * mm});
            skLineSegment(sketch, "E733", {"start": v(3.09, -25.49) * mm, "end": v(3.14, -25.52) * mm});
            skLineSegment(sketch, "E734", {"start": v(3.14, -25.52) * mm, "end": v(3.2, -25.61) * mm});
            skLineSegment(sketch, "E735", {"start": v(3.2, -25.61) * mm, "end": v(3.32, -25.86) * mm});
            skLineSegment(sketch, "E736", {"start": v(3.32, -25.86) * mm, "end": v(3.45, -26.1) * mm});
            skLineSegment(sketch, "E737", {"start": v(3.45, -26.1) * mm, "end": v(3.61, -26.39) * mm});
            skLineSegment(sketch, "E738", {"start": v(3.61, -26.39) * mm, "end": v(3.81, -26.7) * mm});
            skLineSegment(sketch, "E739", {"start": v(3.81, -26.7) * mm, "end": v(4.05, -27.04) * mm});
            skLineSegment(sketch, "E740", {"start": v(4.05, -27.04) * mm, "end": v(4.3, -27.37) * mm});
            skLineSegment(sketch, "E741", {"start": v(4.3, -27.37) * mm, "end": v(4.73, -27.29) * mm});
            skLineSegment(sketch, "E742", {"start": v(4.73, -27.29) * mm, "end": v(5.14, -27.15) * mm});
            skLineSegment(sketch, "E743", {"start": v(5.14, -27.15) * mm, "end": v(5.2, -26.73) * mm});
            skLineSegment(sketch, "E744", {"start": v(5.2, -26.73) * mm, "end": v(5.24, -26.32) * mm});
            skLineSegment(sketch, "E745", {"start": v(5.24, -26.32) * mm, "end": v(5.25, -25.95) * mm});
            skLineSegment(sketch, "E746", {"start": v(5.25, -25.95) * mm, "end": v(5.25, -25.62) * mm});
            skLineSegment(sketch, "E747", {"start": v(5.25, -25.62) * mm, "end": v(5.24, -25.34) * mm});
            skLineSegment(sketch, "E748", {"start": v(5.24, -25.34) * mm, "end": v(5.22, -25.07) * mm});
            skLineSegment(sketch, "E749", {"start": v(5.22, -25.07) * mm, "end": v(5.23, -24.97) * mm});
            skLineSegment(sketch, "E750", {"start": v(5.23, -24.97) * mm, "end": v(5.26, -24.9) * mm});
            skLineSegment(sketch, "E751", {"start": v(5.26, -24.9) * mm, "end": v(6.15, -24.6) * mm});
            skLineSegment(sketch, "E752", {"start": v(6.15, -24.6) * mm, "end": v(6.21, -24.63) * mm});
            skLineSegment(sketch, "E753", {"start": v(6.21, -24.63) * mm, "end": v(6.28, -24.7) * mm});
            skLineSegment(sketch, "E754", {"start": v(6.28, -24.7) * mm, "end": v(6.43, -24.94) * mm});
            skLineSegment(sketch, "E755", {"start": v(6.43, -24.94) * mm, "end": v(6.6, -25.17) * mm});
            skLineSegment(sketch, "E756", {"start": v(6.6, -25.17) * mm, "end": v(6.79, -25.43) * mm});
            skLineSegment(sketch, "E757", {"start": v(6.79, -25.43) * mm, "end": v(7.03, -25.71) * mm});
            skLineSegment(sketch, "E758", {"start": v(7.03, -25.71) * mm, "end": v(7.31, -26.02) * mm});
            skLineSegment(sketch, "E759", {"start": v(7.31, -26.02) * mm, "end": v(7.6, -26.31) * mm});
            skLineSegment(sketch, "E760", {"start": v(7.6, -26.31) * mm, "end": v(8.02, -26.17) * mm});
            skLineSegment(sketch, "E761", {"start": v(8.02, -26.17) * mm, "end": v(8.4, -25.98) * mm});
            skLineSegment(sketch, "E762", {"start": v(8.4, -25.98) * mm, "end": v(8.4, -25.56) * mm});
            skLineSegment(sketch, "E763", {"start": v(8.4, -25.56) * mm, "end": v(8.4, -25.15) * mm});
            skLineSegment(sketch, "E764", {"start": v(8.4, -25.15) * mm, "end": v(8.36, -24.78) * mm});
            skLineSegment(sketch, "E765", {"start": v(8.36, -24.78) * mm, "end": v(8.32, -24.45) * mm});
            skLineSegment(sketch, "E766", {"start": v(8.32, -24.45) * mm, "end": v(8.27, -24.18) * mm});
            skLineSegment(sketch, "E767", {"start": v(8.27, -24.18) * mm, "end": v(8.21, -23.91) * mm});
            skLineSegment(sketch, "E768", {"start": v(8.21, -23.91) * mm, "end": v(8.2, -23.8) * mm});
            skLineSegment(sketch, "E769", {"start": v(8.2, -23.8) * mm, "end": v(8.23, -23.74) * mm});
            skLineSegment(sketch, "E770", {"start": v(8.23, -23.74) * mm, "end": v(9.08, -23.33) * mm});
            skLineSegment(sketch, "E771", {"start": v(9.08, -23.33) * mm, "end": v(9.14, -23.35) * mm});
            skLineSegment(sketch, "E772", {"start": v(9.14, -23.35) * mm, "end": v(9.22, -23.41) * mm});
            skLineSegment(sketch, "E773", {"start": v(9.22, -23.41) * mm, "end": v(9.4, -23.62) * mm});
            skLineSegment(sketch, "E774", {"start": v(9.4, -23.62) * mm, "end": v(9.58, -23.83) * mm});
            skLineSegment(sketch, "E775", {"start": v(9.58, -23.83) * mm, "end": v(9.81, -24.06) * mm});
            skLineSegment(sketch, "E776", {"start": v(9.81, -24.06) * mm, "end": v(10.09, -24.3) * mm});
            skLineSegment(sketch, "E777", {"start": v(10.09, -24.3) * mm, "end": v(10.4, -24.58) * mm});
            skLineSegment(sketch, "E778", {"start": v(10.4, -24.58) * mm, "end": v(10.74, -24.83) * mm});
            skLineSegment(sketch, "E779", {"start": v(10.74, -24.83) * mm, "end": v(11.13, -24.64) * mm});
            skLineSegment(sketch, "E780", {"start": v(11.13, -24.64) * mm, "end": v(11.5, -24.4) * mm});
            skLineSegment(sketch, "E781", {"start": v(11.5, -24.4) * mm, "end": v(11.44, -23.98) * mm});
            skLineSegment(sketch, "E782", {"start": v(11.44, -23.98) * mm, "end": v(11.37, -23.57) * mm});
            skLineSegment(sketch, "E783", {"start": v(11.37, -23.57) * mm, "end": v(11.29, -23.2) * mm});
            skLineSegment(sketch, "E784", {"start": v(11.29, -23.2) * mm, "end": v(11.2, -22.9) * mm});
            skLineSegment(sketch, "E785", {"start": v(11.2, -22.9) * mm, "end": v(11.12, -22.63) * mm});
            skLineSegment(sketch, "E786", {"start": v(11.12, -22.63) * mm, "end": v(11.03, -22.37) * mm});
            skLineSegment(sketch, "E787", {"start": v(11.03, -22.37) * mm, "end": v(11, -22.27) * mm});
            skLineSegment(sketch, "E788", {"start": v(11, -22.27) * mm, "end": v(11.02, -22.2) * mm});
            skLineSegment(sketch, "E789", {"start": v(11.02, -22.2) * mm, "end": v(11.8, -21.68) * mm});
            skLineSegment(sketch, "E790", {"start": v(11.8, -21.68) * mm, "end": v(11.87, -21.69) * mm});
            skLineSegment(sketch, "E791", {"start": v(11.87, -21.69) * mm, "end": v(11.96, -21.75) * mm});
            skLineSegment(sketch, "E792", {"start": v(11.96, -21.75) * mm, "end": v(12.16, -21.93) * mm});
            skLineSegment(sketch, "E793", {"start": v(12.16, -21.93) * mm, "end": v(12.38, -22.11) * mm});
            skLineSegment(sketch, "E794", {"start": v(12.38, -22.11) * mm, "end": v(12.64, -22.3) * mm});
            skLineSegment(sketch, "E795", {"start": v(12.64, -22.3) * mm, "end": v(12.94, -22.52) * mm});
            skLineSegment(sketch, "E796", {"start": v(12.94, -22.52) * mm, "end": v(13.3, -22.74) * mm});
            skLineSegment(sketch, "E797", {"start": v(13.3, -22.74) * mm, "end": v(13.65, -22.95) * mm});
            skLineSegment(sketch, "E798", {"start": v(13.65, -22.95) * mm, "end": v(14.02, -22.71) * mm});
            skLineSegment(sketch, "E799", {"start": v(14.02, -22.71) * mm, "end": v(14.34, -22.43) * mm});
            skLineSegment(sketch, "E800", {"start": v(14.34, -22.43) * mm, "end": v(14.23, -22.02) * mm});
            skLineSegment(sketch, "E801", {"start": v(14.23, -22.02) * mm, "end": v(14.1, -21.62) * mm});
            skLineSegment(sketch, "E802", {"start": v(14.1, -21.62) * mm, "end": v(13.98, -21.27) * mm});
            skLineSegment(sketch, "E803", {"start": v(13.98, -21.27) * mm, "end": v(13.86, -20.97) * mm});
            skLineSegment(sketch, "E804", {"start": v(13.86, -20.97) * mm, "end": v(13.74, -20.72) * mm});
            skLineSegment(sketch, "E805", {"start": v(13.74, -20.72) * mm, "end": v(13.62, -20.48) * mm});
            skLineSegment(sketch, "E806", {"start": v(13.62, -20.48) * mm, "end": v(13.58, -20.38) * mm});
            skLineSegment(sketch, "E807", {"start": v(13.58, -20.38) * mm, "end": v(13.59, -20.31) * mm});
            skLineSegment(sketch, "E808", {"start": v(13.59, -20.31) * mm, "end": v(14.3, -19.69) * mm});
            skLineSegment(sketch, "E809", {"start": v(14.3, -19.69) * mm, "end": v(14.37, -19.7) * mm});
            skLineSegment(sketch, "E810", {"start": v(14.37, -19.7) * mm, "end": v(14.46, -19.74) * mm});
            skLineSegment(sketch, "E811", {"start": v(14.46, -19.74) * mm, "end": v(14.69, -19.9) * mm});
            skLineSegment(sketch, "E812", {"start": v(14.69, -19.9) * mm, "end": v(14.92, -20.04) * mm});
            skLineSegment(sketch, "E813", {"start": v(14.92, -20.04) * mm, "end": v(15.2, -20.2) * mm});
            skLineSegment(sketch, "E814", {"start": v(15.2, -20.2) * mm, "end": v(15.53, -20.37) * mm});
            skLineSegment(sketch, "E815", {"start": v(15.53, -20.37) * mm, "end": v(15.91, -20.55) * mm});
            skLineSegment(sketch, "E816", {"start": v(15.91, -20.55) * mm, "end": v(16.3, -20.7) * mm});
            skLineSegment(sketch, "E817", {"start": v(16.3, -20.7) * mm, "end": v(16.62, -20.42) * mm});
            skLineSegment(sketch, "E818", {"start": v(16.62, -20.42) * mm, "end": v(16.91, -20.1) * mm});
            skLineSegment(sketch, "E819", {"start": v(16.91, -20.1) * mm, "end": v(16.75, -19.7) * mm});
            skLineSegment(sketch, "E820", {"start": v(16.75, -19.7) * mm, "end": v(16.58, -19.33) * mm});
            skLineSegment(sketch, "E821", {"start": v(16.58, -19.33) * mm, "end": v(16.4, -19) * mm});
            skLineSegment(sketch, "E822", {"start": v(16.4, -19) * mm, "end": v(16.24, -18.72) * mm});
            skLineSegment(sketch, "E823", {"start": v(16.24, -18.72) * mm, "end": v(16.1, -18.48) * mm});
            skLineSegment(sketch, "E824", {"start": v(16.1, -18.48) * mm, "end": v(15.94, -18.26) * mm});
            skLineSegment(sketch, "E825", {"start": v(15.94, -18.26) * mm, "end": v(15.9, -18.17) * mm});
            skLineSegment(sketch, "E826", {"start": v(15.9, -18.17) * mm, "end": v(15.89, -18.1) * mm});
            skLineSegment(sketch, "E827", {"start": v(15.89, -18.1) * mm, "end": v(16.51, -17.39) * mm});
            skLineSegment(sketch, "E828", {"start": v(16.51, -17.39) * mm, "end": v(16.58, -17.38) * mm});
            skLineSegment(sketch, "E829", {"start": v(16.58, -17.38) * mm, "end": v(16.68, -17.42) * mm});
            skLineSegment(sketch, "E830", {"start": v(16.68, -17.42) * mm, "end": v(16.92, -17.54) * mm});
            skLineSegment(sketch, "E831", {"start": v(16.92, -17.54) * mm, "end": v(17.17, -17.66) * mm});
            skLineSegment(sketch, "E832", {"start": v(17.17, -17.66) * mm, "end": v(17.47, -17.78) * mm});
            skLineSegment(sketch, "E833", {"start": v(17.47, -17.78) * mm, "end": v(17.82, -17.9) * mm});
            skLineSegment(sketch, "E834", {"start": v(17.82, -17.9) * mm, "end": v(18.22, -18.03) * mm});
            skLineSegment(sketch, "E835", {"start": v(18.22, -18.03) * mm, "end": v(18.63, -18.14) * mm});
            skLineSegment(sketch, "E836", {"start": v(18.63, -18.14) * mm, "end": v(18.91, -17.81) * mm});
            skLineSegment(sketch, "E837", {"start": v(18.91, -17.81) * mm, "end": v(19.15, -17.45) * mm});
            skLineSegment(sketch, "E838", {"start": v(19.15, -17.45) * mm, "end": v(18.94, -17.1) * mm});
            skLineSegment(sketch, "E839", {"start": v(18.94, -17.1) * mm, "end": v(18.72, -16.74) * mm});
            skLineSegment(sketch, "E840", {"start": v(18.72, -16.74) * mm, "end": v(18.5, -16.43) * mm});
            skLineSegment(sketch, "E841", {"start": v(18.5, -16.43) * mm, "end": v(18.31, -16.18) * mm});
            skLineSegment(sketch, "E842", {"start": v(18.31, -16.18) * mm, "end": v(18.13, -15.96) * mm});
            skLineSegment(sketch, "E843", {"start": v(18.13, -15.96) * mm, "end": v(17.95, -15.76) * mm});
            skLineSegment(sketch, "E844", {"start": v(17.95, -15.76) * mm, "end": v(17.9, -15.67) * mm});
            skLineSegment(sketch, "E845", {"start": v(17.9, -15.67) * mm, "end": v(17.88, -15.6) * mm});
            skLineSegment(sketch, "E846", {"start": v(17.88, -15.6) * mm, "end": v(18.4, -14.82) * mm});
            skLineSegment(sketch, "E847", {"start": v(18.4, -14.82) * mm, "end": v(18.47, -14.8) * mm});
            skLineSegment(sketch, "E848", {"start": v(18.47, -14.8) * mm, "end": v(18.57, -14.83) * mm});
            skLineSegment(sketch, "E849", {"start": v(18.57, -14.83) * mm, "end": v(18.83, -14.92) * mm});
            skLineSegment(sketch, "E850", {"start": v(18.83, -14.92) * mm, "end": v(19.1, -15) * mm});
            skLineSegment(sketch, "E851", {"start": v(19.1, -15) * mm, "end": v(19.41, -15.09) * mm});
            skLineSegment(sketch, "E852", {"start": v(19.41, -15.09) * mm, "end": v(19.77, -15.16) * mm});
            skLineSegment(sketch, "E853", {"start": v(19.77, -15.16) * mm, "end": v(20.18, -15.24) * mm});
            skLineSegment(sketch, "E854", {"start": v(20.18, -15.24) * mm, "end": v(20.6, -15.3) * mm});
            skLineSegment(sketch, "E855", {"start": v(20.6, -15.3) * mm, "end": v(20.84, -14.93) * mm});
            skLineSegment(sketch, "E856", {"start": v(20.84, -14.93) * mm, "end": v(21.03, -14.54) * mm});
            skLineSegment(sketch, "E857", {"start": v(21.03, -14.54) * mm, "end": v(20.78, -14.2) * mm});
            skLineSegment(sketch, "E858", {"start": v(20.78, -14.2) * mm, "end": v(20.5, -13.89) * mm});
            skLineSegment(sketch, "E859", {"start": v(20.5, -13.89) * mm, "end": v(20.26, -13.61) * mm});
            skLineSegment(sketch, "E860", {"start": v(20.26, -13.61) * mm, "end": v(20.03, -13.38) * mm});
            skLineSegment(sketch, "E861", {"start": v(20.03, -13.38) * mm, "end": v(19.83, -13.2) * mm});
            skLineSegment(sketch, "E862", {"start": v(19.83, -13.2) * mm, "end": v(19.62, -13.02) * mm});
            skLineSegment(sketch, "E863", {"start": v(19.62, -13.02) * mm, "end": v(19.55, -12.94) * mm});
            skLineSegment(sketch, "E864", {"start": v(19.55, -12.94) * mm, "end": v(19.53, -12.88) * mm});
            skLineSegment(sketch, "E865", {"start": v(19.53, -12.88) * mm, "end": v(19.95, -12.03) * mm});
            skLineSegment(sketch, "E866", {"start": v(19.95, -12.03) * mm, "end": v(20, -12) * mm});
            skLineSegment(sketch, "E867", {"start": v(20, -12) * mm, "end": v(20.11, -12.01) * mm});
            skLineSegment(sketch, "E868", {"start": v(20.11, -12.01) * mm, "end": v(20.38, -12.07) * mm});
            skLineSegment(sketch, "E869", {"start": v(20.38, -12.07) * mm, "end": v(20.66, -12.12) * mm});
            skLineSegment(sketch, "E870", {"start": v(20.66, -12.12) * mm, "end": v(20.98, -12.16) * mm});
            skLineSegment(sketch, "E871", {"start": v(20.98, -12.16) * mm, "end": v(21.35, -12.2) * mm});
            skLineSegment(sketch, "E872", {"start": v(21.35, -12.2) * mm, "end": v(21.76, -12.2) * mm});
            skLineSegment(sketch, "E873", {"start": v(21.76, -12.2) * mm, "end": v(22.18, -12.2) * mm});
            skLineSegment(sketch, "E874", {"start": v(22.18, -12.2) * mm, "end": v(22.37, -11.82) * mm});
            skLineSegment(sketch, "E875", {"start": v(22.37, -11.82) * mm, "end": v(22.51, -11.4) * mm});
            skLineSegment(sketch, "E876", {"start": v(22.51, -11.4) * mm, "end": v(22.22, -11.1) * mm});
            skLineSegment(sketch, "E877", {"start": v(22.22, -11.1) * mm, "end": v(21.91, -10.83) * mm});
            skLineSegment(sketch, "E878", {"start": v(21.91, -10.83) * mm, "end": v(21.63, -10.59) * mm});
            skLineSegment(sketch, "E879", {"start": v(21.63, -10.59) * mm, "end": v(21.37, -10.4) * mm});
            skLineSegment(sketch, "E880", {"start": v(21.37, -10.4) * mm, "end": v(21.14, -10.23) * mm});
            skLineSegment(sketch, "E881", {"start": v(21.14, -10.23) * mm, "end": v(20.91, -10.08) * mm});
            skLineSegment(sketch, "E882", {"start": v(20.91, -10.08) * mm, "end": v(20.83, -10.01) * mm});
            skLineSegment(sketch, "E883", {"start": v(20.83, -10.01) * mm, "end": v(20.8, -9.95) * mm});
            skLineSegment(sketch, "E884", {"start": v(20.8, -9.95) * mm, "end": v(21.1, -9.06) * mm});
            skLineSegment(sketch, "E885", {"start": v(21.1, -9.06) * mm, "end": v(21.17, -9.03) * mm});
            skLineSegment(sketch, "E886", {"start": v(21.17, -9.03) * mm, "end": v(21.27, -9.02) * mm});
            skLineSegment(sketch, "E887", {"start": v(21.27, -9.02) * mm, "end": v(21.55, -9.04) * mm});
            skLineSegment(sketch, "E888", {"start": v(21.55, -9.04) * mm, "end": v(21.82, -9.05) * mm});
            skLineSegment(sketch, "E889", {"start": v(21.82, -9.05) * mm, "end": v(22.15, -9.05) * mm});
            skLineSegment(sketch, "E890", {"start": v(22.15, -9.05) * mm, "end": v(22.52, -9.04) * mm});
            skLineSegment(sketch, "E891", {"start": v(22.52, -9.04) * mm, "end": v(22.93, -9) * mm});
            skLineSegment(sketch, "E892", {"start": v(22.93, -9) * mm, "end": v(23.35, -8.94) * mm});
            skLineSegment(sketch, "E893", {"start": v(23.35, -8.94) * mm, "end": v(23.49, -8.53) * mm});
            skLineSegment(sketch, "E894", {"start": v(23.49, -8.53) * mm, "end": v(23.57, -8.1) * mm});
            skLineSegment(sketch, "E895", {"start": v(23.57, -8.1) * mm, "end": v(23.24, -7.85) * mm});
            skLineSegment(sketch, "E896", {"start": v(23.24, -7.85) * mm, "end": v(22.9, -7.61) * mm});
            skLineSegment(sketch, "E897", {"start": v(22.9, -7.61) * mm, "end": v(22.59, -7.41) * mm});
            skLineSegment(sketch, "E898", {"start": v(22.59, -7.41) * mm, "end": v(22.3, -7.25) * mm});
            skLineSegment(sketch, "E899", {"start": v(22.3, -7.25) * mm, "end": v(22.06, -7.12) * mm});
            skLineSegment(sketch, "E900", {"start": v(22.06, -7.12) * mm, "end": v(21.81, -7) * mm});
            skLineSegment(sketch, "E901", {"start": v(21.81, -7) * mm, "end": v(21.73, -6.94) * mm});
            skLineSegment(sketch, "E902", {"start": v(21.73, -6.94) * mm, "end": v(21.69, -6.89) * mm});
            skLineSegment(sketch, "E903", {"start": v(21.69, -6.89) * mm, "end": v(21.87, -5.96) * mm});
            skLineSegment(sketch, "E904", {"start": v(21.87, -5.96) * mm, "end": v(21.93, -5.92) * mm});
            skLineSegment(sketch, "E905", {"start": v(21.93, -5.92) * mm, "end": v(22.03, -5.9) * mm});
            skLineSegment(sketch, "E906", {"start": v(22.03, -5.9) * mm, "end": v(22.3, -5.89) * mm});
            skLineSegment(sketch, "E907", {"start": v(22.3, -5.89) * mm, "end": v(22.58, -5.86) * mm});
            skLineSegment(sketch, "E908", {"start": v(22.58, -5.86) * mm, "end": v(22.9, -5.82) * mm});
            skLineSegment(sketch, "E909", {"start": v(22.9, -5.82) * mm, "end": v(23.27, -5.75) * mm});
            skLineSegment(sketch, "E910", {"start": v(23.27, -5.75) * mm, "end": v(23.68, -5.66) * mm});
            skLineSegment(sketch, "E911", {"start": v(23.68, -5.66) * mm, "end": v(24.08, -5.55) * mm});
            skLineSegment(sketch, "E912", {"start": v(-1.61, -4.11) * mm, "end": v(-2.13, -4.17) * mm});
            skLineSegment(sketch, "E913", {"start": v(-2.13, -4.17) * mm, "end": v(-2.65, -4.11) * mm});
            skLineSegment(sketch, "E914", {"start": v(-2.65, -4.11) * mm, "end": v(-3.15, -3.95) * mm});
            skLineSegment(sketch, "E915", {"start": v(-3.15, -3.95) * mm, "end": v(-3.6, -3.69) * mm});
            skLineSegment(sketch, "E916", {"start": v(-3.6, -3.69) * mm, "end": v(-4, -3.34) * mm});
            skLineSegment(sketch, "E917", {"start": v(-4, -3.34) * mm, "end": v(-4.3, -2.92) * mm});
            skLineSegment(sketch, "E918", {"start": v(-4.3, -2.92) * mm, "end": v(-4.51, -2.44) * mm});
            skLineSegment(sketch, "E919", {"start": v(-4.51, -2.44) * mm, "end": v(-4.62, -1.93) * mm});
            skLineSegment(sketch, "E920", {"start": v(-4.62, -1.93) * mm, "end": v(-4.62, -1.4) * mm});
            skLineSegment(sketch, "E921", {"start": v(-4.62, -1.4) * mm, "end": v(-4.51, -0.9) * mm});
            skLineSegment(sketch, "E922", {"start": v(-4.51, -0.9) * mm, "end": v(-4.3, -0.42) * mm});
            skLineSegment(sketch, "E923", {"start": v(-4.3, -0.42) * mm, "end": v(-4, 0) * mm});
            skLineSegment(sketch, "E924", {"start": v(-4, 0) * mm, "end": v(-3.6, 0.36) * mm});
            skLineSegment(sketch, "E925", {"start": v(-3.6, 0.36) * mm, "end": v(-3.15, 0.62) * mm});
            skLineSegment(sketch, "E926", {"start": v(-3.15, 0.62) * mm, "end": v(-2.65, 0.78) * mm});
            skLineSegment(sketch, "E927", {"start": v(-2.65, 0.78) * mm, "end": v(-2.13, 0.83) * mm});
            skLineSegment(sketch, "E928", {"start": v(-2.13, 0.83) * mm, "end": v(-1.61, 0.78) * mm});
            skLineSegment(sketch, "E929", {"start": v(-1.61, 0.78) * mm, "end": v(-1.12, 0.62) * mm});
            skLineSegment(sketch, "E930", {"start": v(-1.12, 0.62) * mm, "end": v(-0.66, 0.36) * mm});
            skLineSegment(sketch, "E931", {"start": v(-0.66, 0.36) * mm, "end": v(-0.27, 0) * mm});
            skLineSegment(sketch, "E932", {"start": v(-0.27, 0) * mm, "end": v(-0.12, -0.2) * mm});
            skLineSegment(sketch, "E933", {"start": v(-0.12, -3.13) * mm, "end": v(-0.27, -3.34) * mm});
            skLineSegment(sketch, "E934", {"start": v(-0.27, -3.34) * mm, "end": v(-0.66, -3.69) * mm});
            skLineSegment(sketch, "E935", {"start": v(-0.66, -3.69) * mm, "end": v(-1.12, -3.95) * mm});
            skLineSegment(sketch, "E936", {"start": v(-1.12, -3.95) * mm, "end": v(-1.61, -4.11) * mm});
            skLineSegment(sketch, "E937", {"start": v(24.41, 67.86) * mm, "end": v(22.27, 67.13) * mm});
            skLineSegment(sketch, "E938", {"start": v(22.27, 67.13) * mm, "end": v(22.27, 66.2) * mm});
            skLineSegment(sketch, "E939", {"start": v(22.27, 66.2) * mm, "end": v(24.41, 65.47) * mm});
            skLineSegment(sketch, "E940", {"start": v(24.41, 65.47) * mm, "end": v(24.41, 64.53) * mm});
            skLineSegment(sketch, "E941", {"start": v(24.41, 64.53) * mm, "end": v(22.27, 63.8) * mm});
            skLineSegment(sketch, "E942", {"start": v(22.27, 63.8) * mm, "end": v(22.27, 62.87) * mm});
            skLineSegment(sketch, "E943", {"start": v(22.27, 62.87) * mm, "end": v(24.41, 62.14) * mm});
            skLineSegment(sketch, "E944", {"start": v(24.41, 62.14) * mm, "end": v(24.41, 61.2) * mm});
            skLineSegment(sketch, "E945", {"start": v(24.41, 61.2) * mm, "end": v(22.27, 60.46) * mm});
            skLineSegment(sketch, "E946", {"start": v(22.27, 60.46) * mm, "end": v(22.27, 59.54) * mm});
            skLineSegment(sketch, "E947", {"start": v(22.27, 59.54) * mm, "end": v(24.41, 58.8) * mm});
            skLineSegment(sketch, "E948", {"start": v(24.41, 58.8) * mm, "end": v(24.41, 57.86) * mm});
            skLineSegment(sketch, "E949", {"start": v(24.41, 57.86) * mm, "end": v(22.27, 57.13) * mm});
            skLineSegment(sketch, "E950", {"start": v(22.27, 57.13) * mm, "end": v(22.27, 56.2) * mm});
            skLineSegment(sketch, "E951", {"start": v(22.27, 56.2) * mm, "end": v(24.41, 55.47) * mm});
            skLineSegment(sketch, "E952", {"start": v(24.41, 55.47) * mm, "end": v(24.41, 54.53) * mm});
            skLineSegment(sketch, "E953", {"start": v(24.41, 54.53) * mm, "end": v(22.27, 53.8) * mm});
            skLineSegment(sketch, "E954", {"start": v(22.27, 53.8) * mm, "end": v(22.27, 52.87) * mm});
            skLineSegment(sketch, "E955", {"start": v(22.27, 52.87) * mm, "end": v(24.41, 52.14) * mm});
            skLineSegment(sketch, "E956", {"start": v(24.41, 52.14) * mm, "end": v(24.41, 51.2) * mm});
            skLineSegment(sketch, "E957", {"start": v(24.41, 51.2) * mm, "end": v(22.27, 50.46) * mm});
            skLineSegment(sketch, "E958", {"start": v(22.27, 50.46) * mm, "end": v(22.27, 49.54) * mm});
            skLineSegment(sketch, "E959", {"start": v(22.27, 49.54) * mm, "end": v(24.41, 48.8) * mm});
            skLineSegment(sketch, "E960", {"start": v(24.41, 48.8) * mm, "end": v(24.41, 47.86) * mm});
            skLineSegment(sketch, "E961", {"start": v(24.41, 47.86) * mm, "end": v(22.27, 47.13) * mm});
            skLineSegment(sketch, "E962", {"start": v(22.27, 47.13) * mm, "end": v(22.27, 46.2) * mm});
            skLineSegment(sketch, "E963", {"start": v(22.27, 46.2) * mm, "end": v(24.41, 45.47) * mm});
            skLineSegment(sketch, "E964", {"start": v(24.41, 45.47) * mm, "end": v(24.41, 44.53) * mm});
            skLineSegment(sketch, "E965", {"start": v(24.41, 44.53) * mm, "end": v(22.27, 43.8) * mm});
            skLineSegment(sketch, "E966", {"start": v(22.27, 43.8) * mm, "end": v(22.27, 42.87) * mm});
            skLineSegment(sketch, "E967", {"start": v(22.27, 42.87) * mm, "end": v(24.41, 42.14) * mm});
            skLineSegment(sketch, "E968", {"start": v(24.41, 42.14) * mm, "end": v(24.41, 41.2) * mm});
            skLineSegment(sketch, "E969", {"start": v(24.41, 41.2) * mm, "end": v(22.27, 40.46) * mm});
            skLineSegment(sketch, "E970", {"start": v(22.27, 40.46) * mm, "end": v(22.27, 39.54) * mm});
            skLineSegment(sketch, "E971", {"start": v(22.27, 39.54) * mm, "end": v(24.41, 38.8) * mm});
            skLineSegment(sketch, "E972", {"start": v(24.41, 38.8) * mm, "end": v(24.41, 37.86) * mm});
            skLineSegment(sketch, "E973", {"start": v(24.41, 37.86) * mm, "end": v(22.27, 37.13) * mm});
            skLineSegment(sketch, "E974", {"start": v(22.27, 37.13) * mm, "end": v(22.27, 36.2) * mm});
            skLineSegment(sketch, "E975", {"start": v(22.27, 36.2) * mm, "end": v(24.41, 35.47) * mm});
            skLineSegment(sketch, "E976", {"start": v(24.41, 35.47) * mm, "end": v(24.41, 34.53) * mm});
            skLineSegment(sketch, "E977", {"start": v(24.41, 34.53) * mm, "end": v(22.27, 33.8) * mm});
            skLineSegment(sketch, "E978", {"start": v(22.27, 33.8) * mm, "end": v(22.27, 32.87) * mm});
            skLineSegment(sketch, "E979", {"start": v(22.27, 32.87) * mm, "end": v(24.41, 32.14) * mm});
            skLineSegment(sketch, "E980", {"start": v(24.41, 32.14) * mm, "end": v(24.41, 31.2) * mm});
            skLineSegment(sketch, "E981", {"start": v(24.41, 31.2) * mm, "end": v(22.27, 30.46) * mm});
            skLineSegment(sketch, "E982", {"start": v(22.27, 30.46) * mm, "end": v(22.27, 29.54) * mm});
            skLineSegment(sketch, "E983", {"start": v(22.27, 29.54) * mm, "end": v(24.41, 28.8) * mm});
            skLineSegment(sketch, "E984", {"start": v(24.41, 28.8) * mm, "end": v(24.41, 27.86) * mm});
            skLineSegment(sketch, "E985", {"start": v(24.41, 27.86) * mm, "end": v(22.27, 27.13) * mm});
            skLineSegment(sketch, "E986", {"start": v(22.27, 27.13) * mm, "end": v(22.27, 26.2) * mm});
            skLineSegment(sketch, "E987", {"start": v(22.27, 26.2) * mm, "end": v(24.41, 25.47) * mm});
            skLineSegment(sketch, "E988", {"start": v(24.41, 25.47) * mm, "end": v(24.41, 24.53) * mm});
            skLineSegment(sketch, "E989", {"start": v(24.41, 24.53) * mm, "end": v(22.27, 23.8) * mm});
            skLineSegment(sketch, "E990", {"start": v(22.27, 23.8) * mm, "end": v(22.27, 22.87) * mm});
            skLineSegment(sketch, "E991", {"start": v(22.27, 22.87) * mm, "end": v(24.41, 22.14) * mm});
            skLineSegment(sketch, "E992", {"start": v(24.41, 22.14) * mm, "end": v(24.41, 21.2) * mm});
            skLineSegment(sketch, "E993", {"start": v(24.41, 21.2) * mm, "end": v(22.27, 20.46) * mm});
            skLineSegment(sketch, "E994", {"start": v(22.27, 20.46) * mm, "end": v(22.27, 19.54) * mm});
            skLineSegment(sketch, "E995", {"start": v(22.27, 19.54) * mm, "end": v(24.41, 18.8) * mm});
            skLineSegment(sketch, "E996", {"start": v(24.41, 18.8) * mm, "end": v(24.41, 17.86) * mm});
            skLineSegment(sketch, "E997", {"start": v(24.41, 17.86) * mm, "end": v(22.27, 17.13) * mm});
            skLineSegment(sketch, "E998", {"start": v(22.27, 17.13) * mm, "end": v(22.27, 16.2) * mm});
            skLineSegment(sketch, "E999", {"start": v(22.27, 16.2) * mm, "end": v(24.41, 15.47) * mm});
            skLineSegment(sketch, "E1000", {"start": v(24.41, 15.47) * mm, "end": v(24.41, 14.53) * mm});
            skLineSegment(sketch, "E1001", {"start": v(24.41, 14.53) * mm, "end": v(22.27, 13.8) * mm});
            skLineSegment(sketch, "E1002", {"start": v(22.27, 13.8) * mm, "end": v(22.27, 12.87) * mm});
            skLineSegment(sketch, "E1003", {"start": v(22.27, 12.87) * mm, "end": v(24.41, 12.14) * mm});
            skLineSegment(sketch, "E1004", {"start": v(24.41, 12.14) * mm, "end": v(24.41, 11.2) * mm});
            skLineSegment(sketch, "E1005", {"start": v(24.41, 11.2) * mm, "end": v(22.27, 10.46) * mm});
            skLineSegment(sketch, "E1006", {"start": v(22.27, 10.46) * mm, "end": v(22.27, 9.54) * mm});
            skLineSegment(sketch, "E1007", {"start": v(22.27, 9.54) * mm, "end": v(24.41, 8.8) * mm});
            skLineSegment(sketch, "E1008", {"start": v(24.41, 8.8) * mm, "end": v(24.41, 7.86) * mm});
            skLineSegment(sketch, "E1009", {"start": v(24.41, 7.86) * mm, "end": v(22.27, 7.13) * mm});
            skLineSegment(sketch, "E1010", {"start": v(22.27, 7.13) * mm, "end": v(22.27, 6.2) * mm});
            skLineSegment(sketch, "E1011", {"start": v(22.27, 6.2) * mm, "end": v(24.41, 5.47) * mm});
            skLineSegment(sketch, "E1012", {"start": v(24.41, 5.47) * mm, "end": v(24.41, 4.53) * mm});
            skLineSegment(sketch, "E1013", {"start": v(24.41, 4.53) * mm, "end": v(22.27, 3.8) * mm});
            skLineSegment(sketch, "E1014", {"start": v(22.27, 3.8) * mm, "end": v(22.27, 2.87) * mm});
            skLineSegment(sketch, "E1015", {"start": v(22.27, 2.87) * mm, "end": v(24.41, 2.14) * mm});
            skLineSegment(sketch, "E1016", {"start": v(24.41, 2.14) * mm, "end": v(24.41, 1.2) * mm});
            skLineSegment(sketch, "E1017", {"start": v(24.41, 1.2) * mm, "end": v(22.27, 0.46) * mm});
            skLineSegment(sketch, "E1018", {"start": v(22.27, 0.46) * mm, "end": v(22.27, -0.46) * mm});
            skLineSegment(sketch, "E1019", {"start": v(22.27, -0.46) * mm, "end": v(24.41, -1.2) * mm});
            skLineSegment(sketch, "E1020", {"start": v(24.41, -1.2) * mm, "end": v(24.41, -2.14) * mm});
            skLineSegment(sketch, "E1021", {"start": v(24.41, -2.14) * mm, "end": v(22.27, -2.87) * mm});
            skLineSegment(sketch, "E1022", {"start": v(22.27, -2.87) * mm, "end": v(22.27, -3.8) * mm});
            skLineSegment(sketch, "E1023", {"start": v(22.27, -3.8) * mm, "end": v(24.41, -4.53) * mm});
            skLineSegment(sketch, "E1024", {"start": v(24.41, -4.53) * mm, "end": v(24.41, -5.47) * mm});
            skLineSegment(sketch, "E1025", {"start": v(24.41, -5.47) * mm, "end": v(22.27, -6.2) * mm});
            skLineSegment(sketch, "E1026", {"start": v(22.27, -6.2) * mm, "end": v(22.27, -7.13) * mm});
            skLineSegment(sketch, "E1027", {"start": v(22.27, -7.13) * mm, "end": v(24.41, -7.86) * mm});
            skLineSegment(sketch, "E1028", {"start": v(24.41, -7.86) * mm, "end": v(24.41, -8.8) * mm});
            skLineSegment(sketch, "E1029", {"start": v(24.41, -8.8) * mm, "end": v(22.27, -9.54) * mm});
            skLineSegment(sketch, "E1030", {"start": v(22.27, -9.54) * mm, "end": v(22.27, -10.46) * mm});
            skLineSegment(sketch, "E1031", {"start": v(22.27, -10.46) * mm, "end": v(24.41, -11.2) * mm});
            skLineSegment(sketch, "E1032", {"start": v(24.41, -11.2) * mm, "end": v(24.41, -12.14) * mm});
            skLineSegment(sketch, "E1033", {"start": v(24.41, -12.14) * mm, "end": v(22.27, -12.87) * mm});
            skLineSegment(sketch, "E1034", {"start": v(22.27, -12.87) * mm, "end": v(22.27, -13.8) * mm});
            skLineSegment(sketch, "E1035", {"start": v(22.27, -13.8) * mm, "end": v(24.41, -14.53) * mm});
            skLineSegment(sketch, "E1036", {"start": v(24.41, -14.53) * mm, "end": v(24.41, -15.47) * mm});
            skLineSegment(sketch, "E1037", {"start": v(24.41, -15.47) * mm, "end": v(22.27, -16.2) * mm});
            skLineSegment(sketch, "E1038", {"start": v(22.27, -16.2) * mm, "end": v(22.27, -17.13) * mm});
            skLineSegment(sketch, "E1039", {"start": v(22.27, -17.13) * mm, "end": v(24.41, -17.86) * mm});
            skLineSegment(sketch, "E1040", {"start": v(24.41, -17.86) * mm, "end": v(24.41, -18.8) * mm});
            skLineSegment(sketch, "E1041", {"start": v(24.41, -18.8) * mm, "end": v(22.27, -19.54) * mm});
            skLineSegment(sketch, "E1042", {"start": v(22.27, -19.54) * mm, "end": v(22.27, -20.46) * mm});
            skLineSegment(sketch, "E1043", {"start": v(22.27, -20.46) * mm, "end": v(24.41, -21.2) * mm});
            skLineSegment(sketch, "E1044", {"start": v(24.41, -21.2) * mm, "end": v(24.41, -22.14) * mm});
            skLineSegment(sketch, "E1045", {"start": v(24.41, -22.14) * mm, "end": v(22.27, -22.87) * mm});
            skLineSegment(sketch, "E1046", {"start": v(22.27, -22.87) * mm, "end": v(22.27, -23.8) * mm});
            skLineSegment(sketch, "E1047", {"start": v(22.27, -23.8) * mm, "end": v(24.41, -24.53) * mm});
            skLineSegment(sketch, "E1048", {"start": v(24.41, -24.53) * mm, "end": v(24.41, -25.47) * mm});
            skLineSegment(sketch, "E1049", {"start": v(24.41, -25.47) * mm, "end": v(22.27, -26.2) * mm});
            skLineSegment(sketch, "E1050", {"start": v(22.27, -26.2) * mm, "end": v(22.27, -27.13) * mm});
            skLineSegment(sketch, "E1051", {"start": v(22.27, -27.13) * mm, "end": v(24.41, -27.86) * mm});
            skLineSegment(sketch, "E1052", {"start": v(24.41, -27.86) * mm, "end": v(24.41, -28.8) * mm});
            skLineSegment(sketch, "E1053", {"start": v(24.41, -28.8) * mm, "end": v(22.27, -29.54) * mm});
            skLineSegment(sketch, "E1054", {"start": v(22.27, -29.54) * mm, "end": v(22.27, -30.46) * mm});
            skLineSegment(sketch, "E1055", {"start": v(22.27, -30.46) * mm, "end": v(24.41, -31.2) * mm});
            skLineSegment(sketch, "E1056", {"start": v(24.41, -31.2) * mm, "end": v(24.41, -32.14) * mm});
            skLineSegment(sketch, "E1057", {"start": v(24.41, -32.14) * mm, "end": v(22.27, -32.87) * mm});
            skLineSegment(sketch, "E1058", {"start": v(22.27, -32.87) * mm, "end": v(22.27, -33.8) * mm});
            skLineSegment(sketch, "E1059", {"start": v(22.27, -33.8) * mm, "end": v(24.41, -34.53) * mm});
            skLineSegment(sketch, "E1060", {"start": v(24.41, -34.53) * mm, "end": v(24.41, -35.47) * mm});
            skLineSegment(sketch, "E1061", {"start": v(24.41, -35.47) * mm, "end": v(22.27, -36.2) * mm});
            skLineSegment(sketch, "E1062", {"start": v(22.27, -36.2) * mm, "end": v(22.27, -37.13) * mm});
            skLineSegment(sketch, "E1063", {"start": v(22.27, -37.13) * mm, "end": v(24.41, -37.86) * mm});
            skLineSegment(sketch, "E1064", {"start": v(24.41, -37.86) * mm, "end": v(24.41, -38.8) * mm});
            skLineSegment(sketch, "E1065", {"start": v(24.41, -38.8) * mm, "end": v(22.27, -39.54) * mm});
            skLineSegment(sketch, "E1066", {"start": v(22.27, -39.54) * mm, "end": v(22.27, -40.46) * mm});
            skLineSegment(sketch, "E1067", {"start": v(22.27, -40.46) * mm, "end": v(24.41, -41.2) * mm});
            skLineSegment(sketch, "E1068", {"start": v(24.41, -41.2) * mm, "end": v(24.41, -42.14) * mm});
            skLineSegment(sketch, "E1069", {"start": v(24.41, -42.14) * mm, "end": v(22.27, -42.87) * mm});
            skLineSegment(sketch, "E1070", {"start": v(22.27, -42.87) * mm, "end": v(22.27, -43.8) * mm});
            skLineSegment(sketch, "E1071", {"start": v(22.27, -43.8) * mm, "end": v(24.41, -44.53) * mm});
            skLineSegment(sketch, "E1072", {"start": v(24.41, -44.53) * mm, "end": v(24.41, -45.47) * mm});
            skLineSegment(sketch, "E1073", {"start": v(24.41, -45.47) * mm, "end": v(22.27, -46.2) * mm});
            skLineSegment(sketch, "E1074", {"start": v(22.27, -46.2) * mm, "end": v(22.27, -47.13) * mm});
            skLineSegment(sketch, "E1075", {"start": v(22.27, -47.13) * mm, "end": v(24.41, -47.86) * mm});
            skLineSegment(sketch, "E1076", {"start": v(24.41, -47.86) * mm, "end": v(24.41, -48.8) * mm});
            skLineSegment(sketch, "E1077", {"start": v(24.41, -48.8) * mm, "end": v(22.27, -49.54) * mm});
            skLineSegment(sketch, "E1078", {"start": v(22.27, -49.54) * mm, "end": v(22.27, -50.46) * mm});
            skLineSegment(sketch, "E1079", {"start": v(22.27, -50.46) * mm, "end": v(24.41, -51.2) * mm});
            skLineSegment(sketch, "E1080", {"start": v(24.41, -51.2) * mm, "end": v(24.41, -52.14) * mm});
            skLineSegment(sketch, "E1081", {"start": v(24.41, -52.14) * mm, "end": v(22.27, -52.87) * mm});
            skLineSegment(sketch, "E1082", {"start": v(22.27, -52.87) * mm, "end": v(22.27, -53.8) * mm});
            skLineSegment(sketch, "E1083", {"start": v(22.27, -53.8) * mm, "end": v(24.41, -54.53) * mm});
            skLineSegment(sketch, "E1084", {"start": v(24.41, -54.53) * mm, "end": v(24.41, -55.47) * mm});
            skLineSegment(sketch, "E1085", {"start": v(24.41, -55.47) * mm, "end": v(22.27, -56.2) * mm});
            skLineSegment(sketch, "E1086", {"start": v(22.27, -56.2) * mm, "end": v(22.27, -57.13) * mm});
            skLineSegment(sketch, "E1087", {"start": v(22.27, -57.13) * mm, "end": v(24.41, -57.86) * mm});
            skLineSegment(sketch, "E1088", {"start": v(24.41, -57.86) * mm, "end": v(24.41, -58.8) * mm});
            skLineSegment(sketch, "E1089", {"start": v(24.41, -58.8) * mm, "end": v(22.27, -59.54) * mm});
            skLineSegment(sketch, "E1090", {"start": v(22.27, -59.54) * mm, "end": v(22.27, -60.46) * mm});
            skLineSegment(sketch, "E1091", {"start": v(22.27, -60.46) * mm, "end": v(24.41, -61.2) * mm});
            skLineSegment(sketch, "E1092", {"start": v(24.41, -61.2) * mm, "end": v(24.41, -62.14) * mm});
            skLineSegment(sketch, "E1093", {"start": v(24.41, -62.14) * mm, "end": v(22.27, -62.87) * mm});
            skLineSegment(sketch, "E1094", {"start": v(22.27, -62.87) * mm, "end": v(22.27, -63.8) * mm});
            skLineSegment(sketch, "E1095", {"start": v(22.27, -63.8) * mm, "end": v(24.41, -64.53) * mm});
            skLineSegment(sketch, "E1096", {"start": v(24.41, -64.53) * mm, "end": v(24.41, -65.47) * mm});
            skLineSegment(sketch, "E1097", {"start": v(25.91, 68.33) * mm, "end": v(24.41, 68.33) * mm});
            skLineSegment(sketch, "E1098", {"start": v(24.41, 68.33) * mm, "end": v(24.41, 67.86) * mm});
            skLineSegment(sketch, "E1099", {"start": v(-0.12, -0.2) * mm, "end": v(-0.12, -3.13) * mm});
            skLineSegment(sketch, "E1100.0.1.1", {"start": v(22.27, -73.78) * mm, "end": v(24.41, -74.51) * mm});
            skLineSegment(sketch, "E1100.0.1.2", {"start": v(22.27, -110.45) * mm, "end": v(24.41, -111.18) * mm});
            skLineSegment(sketch, "E1100.0.1.3", {"start": v(24.41, -77.85) * mm, "end": v(24.41, -78.79) * mm});
            skLineSegment(sketch, "E1100.0.1.4", {"start": v(24.41, -75.45) * mm, "end": v(22.27, -76.19) * mm});
            skLineSegment(sketch, "E1100.0.1.5", {"start": v(22.27, -83.78) * mm, "end": v(24.41, -84.51) * mm});
            skLineSegment(sketch, "E1100.0.1.6", {"start": v(22.27, -97.11) * mm, "end": v(24.41, -97.85) * mm});
            skLineSegment(sketch, "E1100.0.1.7", {"start": v(24.41, -91.18) * mm, "end": v(24.41, -92.12) * mm});
            skLineSegment(sketch, "E1100.0.1.8", {"start": v(24.41, -88.79) * mm, "end": v(22.27, -89.52) * mm});
            skLineSegment(sketch, "E1100.0.1.9", {"start": v(24.41, -104.51) * mm, "end": v(24.41, -105.45) * mm});
            skLineSegment(sketch, "E1100.0.1.10", {"start": v(24.41, -102.12) * mm, "end": v(22.27, -102.85) * mm});
            skLineSegment(sketch, "E1100.0.1.11", {"start": v(22.27, -113.78) * mm, "end": v(24.41, -114.51) * mm});
            skLineSegment(sketch, "E1100.0.1.12", {"start": v(24.41, -81.18) * mm, "end": v(24.41, -82.12) * mm});
            skLineSegment(sketch, "E1100.0.1.13", {"start": v(22.27, -87.11) * mm, "end": v(24.41, -87.85) * mm});
            skLineSegment(sketch, "E1100.0.1.14", {"start": v(22.27, -100.45) * mm, "end": v(24.41, -101.18) * mm});
            skLineSegment(sketch, "E1100.0.1.15", {"start": v(24.41, -94.51) * mm, "end": v(24.41, -95.45) * mm});
            skLineSegment(sketch, "E1100.0.1.16", {"start": v(24.41, -107.85) * mm, "end": v(24.41, -108.79) * mm});
            skLineSegment(sketch, "E1100.0.1.17", {"start": v(22.27, -70.45) * mm, "end": v(24.41, -71.18) * mm});
            skLineSegment(sketch, "E1100.0.1.18", {"start": v(24.41, -74.51) * mm, "end": v(24.41, -75.45) * mm});
            skLineSegment(sketch, "E1100.0.1.20", {"start": v(24.41, -82.12) * mm, "end": v(22.27, -82.85) * mm});
            skLineSegment(sketch, "E1100.0.1.21", {"start": v(24.41, -87.85) * mm, "end": v(24.41, -88.79) * mm});
            skLineSegment(sketch, "E1100.0.1.22", {"start": v(24.41, -101.18) * mm, "end": v(24.41, -102.12) * mm});
            skLineSegment(sketch, "E1100.0.1.23", {"start": v(24.41, -95.45) * mm, "end": v(22.27, -96.19) * mm});
            skLineSegment(sketch, "E1100.0.1.24", {"start": v(24.41, -108.79) * mm, "end": v(22.27, -109.52) * mm});
            skLineSegment(sketch, "E1100.0.1.25", {"start": v(24.41, -71.18) * mm, "end": v(24.41, -72.12) * mm});
            skLineSegment(sketch, "E1100.0.1.26", {"start": v(24.41, -111.18) * mm, "end": v(24.41, -112.12) * mm});
            skLineSegment(sketch, "E1100.0.1.27", {"start": v(24.41, -78.79) * mm, "end": v(22.27, -79.52) * mm});
            skLineSegment(sketch, "E1100.0.1.28", {"start": v(22.27, -76.19) * mm, "end": v(22.27, -77.11) * mm});
            skLineSegment(sketch, "E1100.0.1.29", {"start": v(24.41, -84.51) * mm, "end": v(24.41, -85.45) * mm});
            skLineSegment(sketch, "E1100.0.1.30", {"start": v(24.41, -97.85) * mm, "end": v(24.41, -98.79) * mm});
            skLineSegment(sketch, "E1100.0.1.31", {"start": v(24.41, -92.12) * mm, "end": v(22.27, -92.85) * mm});
            skLineSegment(sketch, "E1100.0.1.32", {"start": v(22.27, -89.52) * mm, "end": v(22.27, -90.45) * mm});
            skLineSegment(sketch, "E1100.0.1.33", {"start": v(24.41, -105.45) * mm, "end": v(22.27, -106.19) * mm});
            skLineSegment(sketch, "E1100.0.1.34", {"start": v(22.27, -102.85) * mm, "end": v(22.27, -103.78) * mm});
            skLineSegment(sketch, "E1100.0.1.35", {"start": v(22.27, -82.85) * mm, "end": v(22.27, -83.78) * mm});
            skLineSegment(sketch, "E1100.0.1.36", {"start": v(22.27, -69.52) * mm, "end": v(22.27, -70.45) * mm});
            skLineSegment(sketch, "E1100.0.1.37", {"start": v(22.27, -96.19) * mm, "end": v(22.27, -97.11) * mm});
            skLineSegment(sketch, "E1100.0.1.38", {"start": v(22.27, -109.52) * mm, "end": v(22.27, -110.45) * mm});
            skLineSegment(sketch, "E1100.0.1.39", {"start": v(24.41, -72.12) * mm, "end": v(22.27, -72.85) * mm});
            skLineSegment(sketch, "E1100.0.1.40", {"start": v(24.41, -112.12) * mm, "end": v(22.27, -112.85) * mm});
            skLineSegment(sketch, "E1100.0.1.41", {"start": v(22.27, -79.52) * mm, "end": v(22.27, -80.45) * mm});
            skLineSegment(sketch, "E1100.0.1.42", {"start": v(22.27, -77.11) * mm, "end": v(24.41, -77.85) * mm});
            skLineSegment(sketch, "E1100.0.1.43", {"start": v(24.41, -85.45) * mm, "end": v(22.27, -86.19) * mm});
            skLineSegment(sketch, "E1100.0.1.44", {"start": v(24.41, -98.79) * mm, "end": v(22.27, -99.52) * mm});
            skLineSegment(sketch, "E1100.0.1.45", {"start": v(22.27, -90.45) * mm, "end": v(24.41, -91.18) * mm});
            skLineSegment(sketch, "E1100.0.1.46", {"start": v(22.27, -92.85) * mm, "end": v(22.27, -93.78) * mm});
            skLineSegment(sketch, "E1100.0.1.47", {"start": v(22.27, -106.19) * mm, "end": v(22.27, -107.11) * mm});
            skLineSegment(sketch, "E1100.0.1.48", {"start": v(22.27, -103.78) * mm, "end": v(24.41, -104.51) * mm});
            skLineSegment(sketch, "E1100.0.1.49", {"start": v(22.27, -72.85) * mm, "end": v(22.27, -73.78) * mm});
            skLineSegment(sketch, "E1100.0.1.50", {"start": v(22.27, -112.85) * mm, "end": v(22.27, -113.78) * mm});
            skLineSegment(sketch, "E1100.0.1.51", {"start": v(22.27, -80.45) * mm, "end": v(24.41, -81.18) * mm});
            skLineSegment(sketch, "E1100.0.1.52", {"start": v(22.27, -86.19) * mm, "end": v(22.27, -87.11) * mm});
            skLineSegment(sketch, "E1100.0.1.53", {"start": v(22.27, -99.52) * mm, "end": v(22.27, -100.45) * mm});
            skLineSegment(sketch, "E1100.0.1.54", {"start": v(22.27, -93.78) * mm, "end": v(24.41, -94.51) * mm});
            skLineSegment(sketch, "E1100.0.1.55", {"start": v(22.27, -107.11) * mm, "end": v(24.41, -107.85) * mm});
            skLineSegment(sketch, "E1100.0.1.56", {"start": v(24.41, -68.79) * mm, "end": v(22.27, -69.52) * mm});
            skLineSegment(sketch, "E1100.0.2.1", {"start": v(22.27, -120.43) * mm, "end": v(24.41, -121.16) * mm});
            skLineSegment(sketch, "E1100.0.2.2", {"start": v(22.27, -157.1) * mm, "end": v(24.41, -157.83) * mm});
            skLineSegment(sketch, "E1100.0.2.3", {"start": v(24.41, -124.5) * mm, "end": v(24.41, -125.44) * mm});
            skLineSegment(sketch, "E1100.0.2.4", {"start": v(24.41, -122.1) * mm, "end": v(22.27, -122.84) * mm});
            skLineSegment(sketch, "E1100.0.2.5", {"start": v(22.27, -130.43) * mm, "end": v(24.41, -131.16) * mm});
            skLineSegment(sketch, "E1100.0.2.6", {"start": v(22.27, -143.76) * mm, "end": v(24.41, -144.5) * mm});
            skLineSegment(sketch, "E1100.0.2.7", {"start": v(24.41, -137.83) * mm, "end": v(24.41, -138.77) * mm});
            skLineSegment(sketch, "E1100.0.2.8", {"start": v(24.41, -135.44) * mm, "end": v(22.27, -136.17) * mm});
            skLineSegment(sketch, "E1100.0.2.9", {"start": v(24.41, -151.16) * mm, "end": v(24.41, -152.1) * mm});
            skLineSegment(sketch, "E1100.0.2.10", {"start": v(24.41, -148.77) * mm, "end": v(22.27, -149.5) * mm});
            skLineSegment(sketch, "E1100.0.2.11", {"start": v(22.27, -160.43) * mm, "end": v(24.41, -161.16) * mm});
            skLineSegment(sketch, "E1100.0.2.12", {"start": v(24.41, -127.83) * mm, "end": v(24.41, -128.77) * mm});
            skLineSegment(sketch, "E1100.0.2.13", {"start": v(22.27, -133.76) * mm, "end": v(24.41, -134.5) * mm});
            skLineSegment(sketch, "E1100.0.2.14", {"start": v(22.27, -147.1) * mm, "end": v(24.41, -147.83) * mm});
            skLineSegment(sketch, "E1100.0.2.15", {"start": v(24.41, -141.16) * mm, "end": v(24.41, -142.1) * mm});
            skLineSegment(sketch, "E1100.0.2.16", {"start": v(24.41, -154.5) * mm, "end": v(24.41, -155.44) * mm});
            skLineSegment(sketch, "E1100.0.2.17", {"start": v(22.27, -117.1) * mm, "end": v(24.41, -117.83) * mm});
            skLineSegment(sketch, "E1100.0.2.18", {"start": v(24.41, -121.16) * mm, "end": v(24.41, -122.1) * mm});
            skLineSegment(sketch, "E1100.0.2.20", {"start": v(24.41, -128.77) * mm, "end": v(22.27, -129.5) * mm});
            skLineSegment(sketch, "E1100.0.2.21", {"start": v(24.41, -134.5) * mm, "end": v(24.41, -135.44) * mm});
            skLineSegment(sketch, "E1100.0.2.22", {"start": v(24.41, -147.83) * mm, "end": v(24.41, -148.77) * mm});
            skLineSegment(sketch, "E1100.0.2.23", {"start": v(24.41, -142.1) * mm, "end": v(22.27, -142.84) * mm});
            skLineSegment(sketch, "E1100.0.2.24", {"start": v(24.41, -155.44) * mm, "end": v(22.27, -156.17) * mm});
            skLineSegment(sketch, "E1100.0.2.25", {"start": v(24.41, -117.83) * mm, "end": v(24.41, -118.77) * mm});
            skLineSegment(sketch, "E1100.0.2.26", {"start": v(24.41, -157.83) * mm, "end": v(24.41, -158.77) * mm});
            skLineSegment(sketch, "E1100.0.2.27", {"start": v(24.41, -125.44) * mm, "end": v(22.27, -126.17) * mm});
            skLineSegment(sketch, "E1100.0.2.28", {"start": v(22.27, -122.84) * mm, "end": v(22.27, -123.76) * mm});
            skLineSegment(sketch, "E1100.0.2.29", {"start": v(24.41, -131.16) * mm, "end": v(24.41, -132.1) * mm});
            skLineSegment(sketch, "E1100.0.2.30", {"start": v(24.41, -144.5) * mm, "end": v(24.41, -145.44) * mm});
            skLineSegment(sketch, "E1100.0.2.31", {"start": v(24.41, -138.77) * mm, "end": v(22.27, -139.5) * mm});
            skLineSegment(sketch, "E1100.0.2.32", {"start": v(22.27, -136.17) * mm, "end": v(22.27, -137.1) * mm});
            skLineSegment(sketch, "E1100.0.2.33", {"start": v(24.41, -152.1) * mm, "end": v(22.27, -152.84) * mm});
            skLineSegment(sketch, "E1100.0.2.34", {"start": v(22.27, -149.5) * mm, "end": v(22.27, -150.43) * mm});
            skLineSegment(sketch, "E1100.0.2.35", {"start": v(22.27, -129.5) * mm, "end": v(22.27, -130.43) * mm});
            skLineSegment(sketch, "E1100.0.2.36", {"start": v(22.27, -116.17) * mm, "end": v(22.27, -117.1) * mm});
            skLineSegment(sketch, "E1100.0.2.37", {"start": v(22.27, -142.84) * mm, "end": v(22.27, -143.76) * mm});
            skLineSegment(sketch, "E1100.0.2.38", {"start": v(22.27, -156.17) * mm, "end": v(22.27, -157.1) * mm});
            skLineSegment(sketch, "E1100.0.2.39", {"start": v(24.41, -118.77) * mm, "end": v(22.27, -119.5) * mm});
            skLineSegment(sketch, "E1100.0.2.40", {"start": v(24.41, -158.77) * mm, "end": v(22.27, -159.5) * mm});
            skLineSegment(sketch, "E1100.0.2.41", {"start": v(22.27, -126.17) * mm, "end": v(22.27, -127.1) * mm});
            skLineSegment(sketch, "E1100.0.2.42", {"start": v(22.27, -123.76) * mm, "end": v(24.41, -124.5) * mm});
            skLineSegment(sketch, "E1100.0.2.43", {"start": v(24.41, -132.1) * mm, "end": v(22.27, -132.84) * mm});
            skLineSegment(sketch, "E1100.0.2.44", {"start": v(24.41, -145.44) * mm, "end": v(22.27, -146.17) * mm});
            skLineSegment(sketch, "E1100.0.2.45", {"start": v(22.27, -137.1) * mm, "end": v(24.41, -137.83) * mm});
            skLineSegment(sketch, "E1100.0.2.46", {"start": v(22.27, -139.5) * mm, "end": v(22.27, -140.43) * mm});
            skLineSegment(sketch, "E1100.0.2.47", {"start": v(22.27, -152.84) * mm, "end": v(22.27, -153.76) * mm});
            skLineSegment(sketch, "E1100.0.2.48", {"start": v(22.27, -150.43) * mm, "end": v(24.41, -151.16) * mm});
            skLineSegment(sketch, "E1100.0.2.49", {"start": v(22.27, -119.5) * mm, "end": v(22.27, -120.43) * mm});
            skLineSegment(sketch, "E1100.0.2.50", {"start": v(22.27, -159.5) * mm, "end": v(22.27, -160.43) * mm});
            skLineSegment(sketch, "E1100.0.2.51", {"start": v(22.27, -127.1) * mm, "end": v(24.41, -127.83) * mm});
            skLineSegment(sketch, "E1100.0.2.52", {"start": v(22.27, -132.84) * mm, "end": v(22.27, -133.76) * mm});
            skLineSegment(sketch, "E1100.0.2.53", {"start": v(22.27, -146.17) * mm, "end": v(22.27, -147.1) * mm});
            skLineSegment(sketch, "E1100.0.2.54", {"start": v(22.27, -140.43) * mm, "end": v(24.41, -141.16) * mm});
            skLineSegment(sketch, "E1100.0.2.55", {"start": v(22.27, -153.76) * mm, "end": v(24.41, -154.5) * mm});
            skLineSegment(sketch, "E1100.0.2.56", {"start": v(24.41, -115.44) * mm, "end": v(22.27, -116.17) * mm});
            skLineSegment(sketch, "E1100.0.3.1", {"start": v(22.27, -167.08) * mm, "end": v(24.41, -167.81) * mm});
            skLineSegment(sketch, "E1100.0.3.2", {"start": v(22.27, -203.75) * mm, "end": v(24.41, -204.48) * mm});
            skLineSegment(sketch, "E1100.0.3.3", {"start": v(24.41, -171.15) * mm, "end": v(24.41, -172.09) * mm});
            skLineSegment(sketch, "E1100.0.3.4", {"start": v(24.41, -168.75) * mm, "end": v(22.27, -169.49) * mm});
            skLineSegment(sketch, "E1100.0.3.5", {"start": v(22.27, -177.08) * mm, "end": v(24.41, -177.81) * mm});
            skLineSegment(sketch, "E1100.0.3.6", {"start": v(22.27, -190.41) * mm, "end": v(24.41, -191.15) * mm});
            skLineSegment(sketch, "E1100.0.3.7", {"start": v(24.41, -184.48) * mm, "end": v(24.41, -185.42) * mm});
            skLineSegment(sketch, "E1100.0.3.8", {"start": v(24.41, -182.09) * mm, "end": v(22.27, -182.82) * mm});
            skLineSegment(sketch, "E1100.0.3.9", {"start": v(24.41, -197.81) * mm, "end": v(24.41, -198.75) * mm});
            skLineSegment(sketch, "E1100.0.3.10", {"start": v(24.41, -195.42) * mm, "end": v(22.27, -196.15) * mm});
            skLineSegment(sketch, "E1100.0.3.11", {"start": v(22.27, -207.08) * mm, "end": v(24.41, -207.81) * mm});
            skLineSegment(sketch, "E1100.0.3.12", {"start": v(24.41, -174.48) * mm, "end": v(24.41, -175.42) * mm});
            skLineSegment(sketch, "E1100.0.3.13", {"start": v(22.27, -180.41) * mm, "end": v(24.41, -181.15) * mm});
            skLineSegment(sketch, "E1100.0.3.14", {"start": v(22.27, -193.75) * mm, "end": v(24.41, -194.48) * mm});
            skLineSegment(sketch, "E1100.0.3.15", {"start": v(24.41, -187.81) * mm, "end": v(24.41, -188.75) * mm});
            skLineSegment(sketch, "E1100.0.3.16", {"start": v(24.41, -201.15) * mm, "end": v(24.41, -202.09) * mm});
            skLineSegment(sketch, "E1100.0.3.17", {"start": v(22.27, -163.75) * mm, "end": v(24.41, -164.48) * mm});
            skLineSegment(sketch, "E1100.0.3.18", {"start": v(24.41, -167.81) * mm, "end": v(24.41, -168.75) * mm});
            skLineSegment(sketch, "E1100.0.3.20", {"start": v(24.41, -175.42) * mm, "end": v(22.27, -176.15) * mm});
            skLineSegment(sketch, "E1100.0.3.21", {"start": v(24.41, -181.15) * mm, "end": v(24.41, -182.09) * mm});
            skLineSegment(sketch, "E1100.0.3.22", {"start": v(24.41, -194.48) * mm, "end": v(24.41, -195.42) * mm});
            skLineSegment(sketch, "E1100.0.3.23", {"start": v(24.41, -188.75) * mm, "end": v(22.27, -189.49) * mm});
            skLineSegment(sketch, "E1100.0.3.24", {"start": v(24.41, -202.09) * mm, "end": v(22.27, -202.82) * mm});
            skLineSegment(sketch, "E1100.0.3.25", {"start": v(24.41, -164.48) * mm, "end": v(24.41, -165.42) * mm});
            skLineSegment(sketch, "E1100.0.3.26", {"start": v(24.41, -204.48) * mm, "end": v(24.41, -205.42) * mm});
            skLineSegment(sketch, "E1100.0.3.27", {"start": v(24.41, -172.09) * mm, "end": v(22.27, -172.82) * mm});
            skLineSegment(sketch, "E1100.0.3.28", {"start": v(22.27, -169.49) * mm, "end": v(22.27, -170.41) * mm});
            skLineSegment(sketch, "E1100.0.3.29", {"start": v(24.41, -177.81) * mm, "end": v(24.41, -178.75) * mm});
            skLineSegment(sketch, "E1100.0.3.30", {"start": v(24.41, -191.15) * mm, "end": v(24.41, -192.09) * mm});
            skLineSegment(sketch, "E1100.0.3.31", {"start": v(24.41, -185.42) * mm, "end": v(22.27, -186.15) * mm});
            skLineSegment(sketch, "E1100.0.3.32", {"start": v(22.27, -182.82) * mm, "end": v(22.27, -183.75) * mm});
            skLineSegment(sketch, "E1100.0.3.33", {"start": v(24.41, -198.75) * mm, "end": v(22.27, -199.49) * mm});
            skLineSegment(sketch, "E1100.0.3.34", {"start": v(22.27, -196.15) * mm, "end": v(22.27, -197.08) * mm});
            skLineSegment(sketch, "E1100.0.3.35", {"start": v(22.27, -176.15) * mm, "end": v(22.27, -177.08) * mm});
            skLineSegment(sketch, "E1100.0.3.36", {"start": v(22.27, -162.82) * mm, "end": v(22.27, -163.75) * mm});
            skLineSegment(sketch, "E1100.0.3.37", {"start": v(22.27, -189.49) * mm, "end": v(22.27, -190.41) * mm});
            skLineSegment(sketch, "E1100.0.3.38", {"start": v(22.27, -202.82) * mm, "end": v(22.27, -203.75) * mm});
            skLineSegment(sketch, "E1100.0.3.39", {"start": v(24.41, -165.42) * mm, "end": v(22.27, -166.15) * mm});
            skLineSegment(sketch, "E1100.0.3.40", {"start": v(24.41, -205.42) * mm, "end": v(22.27, -206.15) * mm});
            skLineSegment(sketch, "E1100.0.3.41", {"start": v(22.27, -172.82) * mm, "end": v(22.27, -173.75) * mm});
            skLineSegment(sketch, "E1100.0.3.42", {"start": v(22.27, -170.41) * mm, "end": v(24.41, -171.15) * mm});
            skLineSegment(sketch, "E1100.0.3.43", {"start": v(24.41, -178.75) * mm, "end": v(22.27, -179.49) * mm});
            skLineSegment(sketch, "E1100.0.3.44", {"start": v(24.41, -192.09) * mm, "end": v(22.27, -192.82) * mm});
            skLineSegment(sketch, "E1100.0.3.45", {"start": v(22.27, -183.75) * mm, "end": v(24.41, -184.48) * mm});
            skLineSegment(sketch, "E1100.0.3.46", {"start": v(22.27, -186.15) * mm, "end": v(22.27, -187.08) * mm});
            skLineSegment(sketch, "E1100.0.3.47", {"start": v(22.27, -199.49) * mm, "end": v(22.27, -200.41) * mm});
            skLineSegment(sketch, "E1100.0.3.48", {"start": v(22.27, -197.08) * mm, "end": v(24.41, -197.81) * mm});
            skLineSegment(sketch, "E1100.0.3.49", {"start": v(22.27, -166.15) * mm, "end": v(22.27, -167.08) * mm});
            skLineSegment(sketch, "E1100.0.3.50", {"start": v(22.27, -206.15) * mm, "end": v(22.27, -207.08) * mm});
            skLineSegment(sketch, "E1100.0.3.51", {"start": v(22.27, -173.75) * mm, "end": v(24.41, -174.48) * mm});
            skLineSegment(sketch, "E1100.0.3.52", {"start": v(22.27, -179.49) * mm, "end": v(22.27, -180.41) * mm});
            skLineSegment(sketch, "E1100.0.3.53", {"start": v(22.27, -192.82) * mm, "end": v(22.27, -193.75) * mm});
            skLineSegment(sketch, "E1100.0.3.54", {"start": v(22.27, -187.08) * mm, "end": v(24.41, -187.81) * mm});
            skLineSegment(sketch, "E1100.0.3.55", {"start": v(22.27, -200.41) * mm, "end": v(24.41, -201.15) * mm});
            skLineSegment(sketch, "E1100.0.3.56", {"start": v(24.41, -162.09) * mm, "end": v(22.27, -162.82) * mm});
            skLineSegment(sketch, "E1100.0.4.0", {"start": v(24.41, -254.93) * mm, "end": v(25.91, -254.93) * mm});
            skLineSegment(sketch, "E1100.0.4.1", {"start": v(22.27, -213.73) * mm, "end": v(24.41, -214.46) * mm});
            skLineSegment(sketch, "E1100.0.4.2", {"start": v(22.27, -250.4) * mm, "end": v(24.41, -251.13) * mm});
            skLineSegment(sketch, "E1100.0.4.3", {"start": v(24.41, -217.8) * mm, "end": v(24.41, -218.74) * mm});
            skLineSegment(sketch, "E1100.0.4.4", {"start": v(24.41, -215.4) * mm, "end": v(22.27, -216.14) * mm});
            skLineSegment(sketch, "E1100.0.4.5", {"start": v(22.27, -223.73) * mm, "end": v(24.41, -224.46) * mm});
            skLineSegment(sketch, "E1100.0.4.6", {"start": v(22.27, -237.06) * mm, "end": v(24.41, -237.8) * mm});
            skLineSegment(sketch, "E1100.0.4.7", {"start": v(24.41, -231.13) * mm, "end": v(24.41, -232.07) * mm});
            skLineSegment(sketch, "E1100.0.4.8", {"start": v(24.41, -228.74) * mm, "end": v(22.27, -229.47) * mm});
            skLineSegment(sketch, "E1100.0.4.9", {"start": v(24.41, -244.46) * mm, "end": v(24.41, -245.4) * mm});
            skLineSegment(sketch, "E1100.0.4.10", {"start": v(24.41, -242.07) * mm, "end": v(22.27, -242.8) * mm});
            skLineSegment(sketch, "E1100.0.4.11", {"start": v(22.27, -253.73) * mm, "end": v(24.41, -254.46) * mm});
            skLineSegment(sketch, "E1100.0.4.12", {"start": v(24.41, -221.13) * mm, "end": v(24.41, -222.07) * mm});
            skLineSegment(sketch, "E1100.0.4.13", {"start": v(22.27, -227.06) * mm, "end": v(24.41, -227.8) * mm});
            skLineSegment(sketch, "E1100.0.4.14", {"start": v(22.27, -240.4) * mm, "end": v(24.41, -241.13) * mm});
            skLineSegment(sketch, "E1100.0.4.15", {"start": v(24.41, -234.46) * mm, "end": v(24.41, -235.4) * mm});
            skLineSegment(sketch, "E1100.0.4.16", {"start": v(24.41, -247.8) * mm, "end": v(24.41, -248.74) * mm});
            skLineSegment(sketch, "E1100.0.4.17", {"start": v(22.27, -210.4) * mm, "end": v(24.41, -211.13) * mm});
            skLineSegment(sketch, "E1100.0.4.18", {"start": v(24.41, -214.46) * mm, "end": v(24.41, -215.4) * mm});
            skLineSegment(sketch, "E1100.0.4.19", {"start": v(24.41, -254.46) * mm, "end": v(24.41, -254.93) * mm});
            skLineSegment(sketch, "E1100.0.4.20", {"start": v(24.41, -222.07) * mm, "end": v(22.27, -222.8) * mm});
            skLineSegment(sketch, "E1100.0.4.21", {"start": v(24.41, -227.8) * mm, "end": v(24.41, -228.74) * mm});
            skLineSegment(sketch, "E1100.0.4.22", {"start": v(24.41, -241.13) * mm, "end": v(24.41, -242.07) * mm});
            skLineSegment(sketch, "E1100.0.4.23", {"start": v(24.41, -235.4) * mm, "end": v(22.27, -236.14) * mm});
            skLineSegment(sketch, "E1100.0.4.24", {"start": v(24.41, -248.74) * mm, "end": v(22.27, -249.47) * mm});
            skLineSegment(sketch, "E1100.0.4.25", {"start": v(24.41, -211.13) * mm, "end": v(24.41, -212.07) * mm});
            skLineSegment(sketch, "E1100.0.4.26", {"start": v(24.41, -251.13) * mm, "end": v(24.41, -252.07) * mm});
            skLineSegment(sketch, "E1100.0.4.27", {"start": v(24.41, -218.74) * mm, "end": v(22.27, -219.47) * mm});
            skLineSegment(sketch, "E1100.0.4.28", {"start": v(22.27, -216.14) * mm, "end": v(22.27, -217.06) * mm});
            skLineSegment(sketch, "E1100.0.4.29", {"start": v(24.41, -224.46) * mm, "end": v(24.41, -225.4) * mm});
            skLineSegment(sketch, "E1100.0.4.30", {"start": v(24.41, -237.8) * mm, "end": v(24.41, -238.74) * mm});
            skLineSegment(sketch, "E1100.0.4.31", {"start": v(24.41, -232.07) * mm, "end": v(22.27, -232.8) * mm});
            skLineSegment(sketch, "E1100.0.4.32", {"start": v(22.27, -229.47) * mm, "end": v(22.27, -230.4) * mm});
            skLineSegment(sketch, "E1100.0.4.33", {"start": v(24.41, -245.4) * mm, "end": v(22.27, -246.14) * mm});
            skLineSegment(sketch, "E1100.0.4.34", {"start": v(22.27, -242.8) * mm, "end": v(22.27, -243.73) * mm});
            skLineSegment(sketch, "E1100.0.4.35", {"start": v(22.27, -222.8) * mm, "end": v(22.27, -223.73) * mm});
            skLineSegment(sketch, "E1100.0.4.36", {"start": v(22.27, -209.47) * mm, "end": v(22.27, -210.4) * mm});
            skLineSegment(sketch, "E1100.0.4.37", {"start": v(22.27, -236.14) * mm, "end": v(22.27, -237.06) * mm});
            skLineSegment(sketch, "E1100.0.4.38", {"start": v(22.27, -249.47) * mm, "end": v(22.27, -250.4) * mm});
            skLineSegment(sketch, "E1100.0.4.39", {"start": v(24.41, -212.07) * mm, "end": v(22.27, -212.8) * mm});
            skLineSegment(sketch, "E1100.0.4.40", {"start": v(24.41, -252.07) * mm, "end": v(22.27, -252.8) * mm});
            skLineSegment(sketch, "E1100.0.4.41", {"start": v(22.27, -219.47) * mm, "end": v(22.27, -220.4) * mm});
            skLineSegment(sketch, "E1100.0.4.42", {"start": v(22.27, -217.06) * mm, "end": v(24.41, -217.8) * mm});
            skLineSegment(sketch, "E1100.0.4.43", {"start": v(24.41, -225.4) * mm, "end": v(22.27, -226.14) * mm});
            skLineSegment(sketch, "E1100.0.4.44", {"start": v(24.41, -238.74) * mm, "end": v(22.27, -239.47) * mm});
            skLineSegment(sketch, "E1100.0.4.45", {"start": v(22.27, -230.4) * mm, "end": v(24.41, -231.13) * mm});
            skLineSegment(sketch, "E1100.0.4.46", {"start": v(22.27, -232.8) * mm, "end": v(22.27, -233.73) * mm});
            skLineSegment(sketch, "E1100.0.4.47", {"start": v(22.27, -246.14) * mm, "end": v(22.27, -247.06) * mm});
            skLineSegment(sketch, "E1100.0.4.48", {"start": v(22.27, -243.73) * mm, "end": v(24.41, -244.46) * mm});
            skLineSegment(sketch, "E1100.0.4.49", {"start": v(22.27, -212.8) * mm, "end": v(22.27, -213.73) * mm});
            skLineSegment(sketch, "E1100.0.4.50", {"start": v(22.27, -252.8) * mm, "end": v(22.27, -253.73) * mm});
            skLineSegment(sketch, "E1100.0.4.51", {"start": v(22.27, -220.4) * mm, "end": v(24.41, -221.13) * mm});
            skLineSegment(sketch, "E1100.0.4.52", {"start": v(22.27, -226.14) * mm, "end": v(22.27, -227.06) * mm});
            skLineSegment(sketch, "E1100.0.4.53", {"start": v(22.27, -239.47) * mm, "end": v(22.27, -240.4) * mm});
            skLineSegment(sketch, "E1100.0.4.54", {"start": v(22.27, -233.73) * mm, "end": v(24.41, -234.46) * mm});
            skLineSegment(sketch, "E1100.0.4.55", {"start": v(22.27, -247.06) * mm, "end": v(24.41, -247.8) * mm});
            skLineSegment(sketch, "E1100.0.4.56", {"start": v(24.41, -208.74) * mm, "end": v(22.27, -209.47) * mm});
            skLineSegment(sketch, "E1100.direction1", {"start": v(24.41, -68.33) * mm, "end": v(49.41, -68.33) * mm, "construction": true});
            skLineSegment(sketch, "E1100.direction2", {"start": v(24.41, -68.33) * mm, "end": v(24.41, -114.98) * mm, "construction": true});
            skLineSegment(sketch, "E1101", {"start": v(24.41, -115.44) * mm, "end": v(24.41, -114.51) * mm});
            skLineSegment(sketch, "E1102", {"start": v(24.41, -67.86) * mm, "end": v(24.41, -68.79) * mm});
            skLineSegment(sketch, "E1103", {"start": v(24.41, -161.16) * mm, "end": v(24.41, -162.09) * mm});
            skLineSegment(sketch, "E1104", {"start": v(24.41, -207.81) * mm, "end": v(24.41, -208.74) * mm});
            skLineSegment(sketch, "E1105", {"start": v(25.91, 68.33) * mm, "end": v(25.91, -65.47) * mm});
            skLineSegment(sketch, "E1106", {"start": v(24.41, -67.86) * mm, "end": v(25.91, -67.86) * mm});
            skLineSegment(sketch, "E1107", {"start": v(24.41, -65.47) * mm, "end": v(25.91, -65.47) * mm});
            skLineSegment(sketch, "E1108.trimOffspring", {"start": v(25.91, -67.86) * mm, "end": v(25.91, -254.93) * mm});
            skSolve(sketch);
        }
        {
            var Q0;
            Q0 = qSketchRegion(id + "F0", true);
            extrude(context, id + "F1", {"entities" : qUnion([Q0]), "depth" : 6 * mm});
        }
    });
